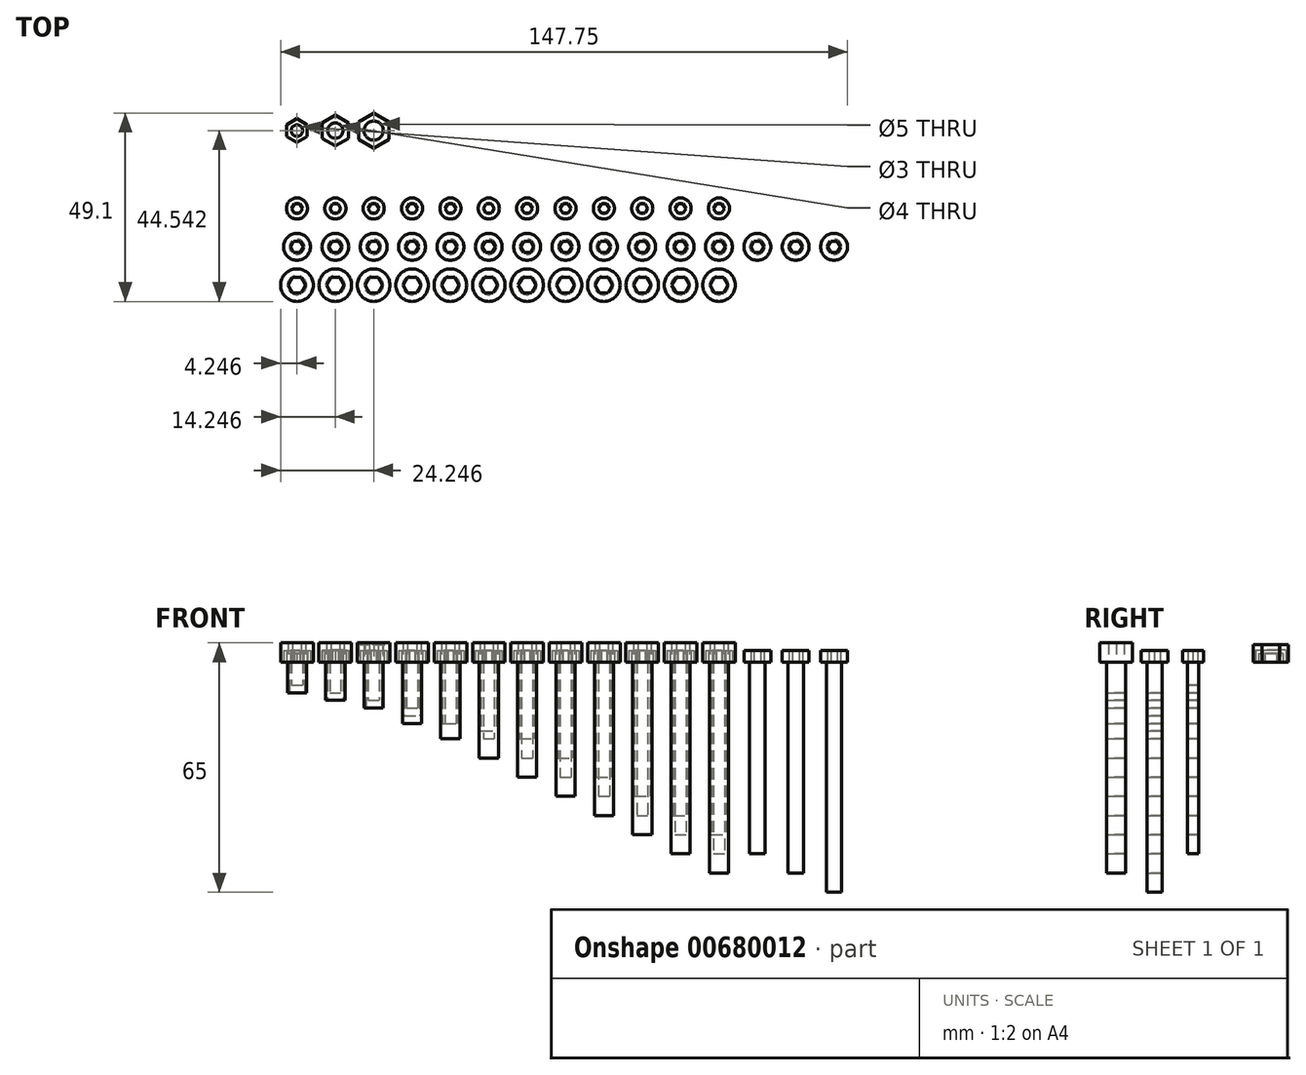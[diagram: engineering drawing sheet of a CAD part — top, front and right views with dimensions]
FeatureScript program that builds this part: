
annotation { "Feature Type Name" : "Feature", "Feature Type Description" : "" }
export const myFeature = defineFeature(function(context is Context, id is Id, definition is map)
    precondition{}
    {
        {
            var Q0;
            Q0=qCreatedBy(makeId("Top.planeOp"),FACE);
            var sketch = newSketch(context, id + "F0", { "sketchPlane" : qUnion([Q0])});
            skCircle(sketch, "E0", {"center": v(10, 10.3) * mm, "radius": 1.5 * mm});
            skLineSegment(sketch, "E1", {"start": v(0, 0) * mm, "end": v(0, 10) * mm, "construction": true});
            skLineSegment(sketch, "E2", {"start": v(0, 10) * mm, "end": v(10, 10.3) * mm, "construction": true});
            skLineSegment(sketch, "E3", {"start": v(10, 10.3) * mm, "end": v(20, 10.3) * mm, "construction": true});
            skLineSegment(sketch, "E4", {"start": v(20, 10.3) * mm, "end": v(30, 10.3) * mm, "construction": true});
            skLineSegment(sketch, "E5", {"start": v(30, 10.3) * mm, "end": v(40, 10.3) * mm, "construction": true});
            skCircle(sketch, "E6", {"center": v(20, 10.3) * mm, "radius": 2 * mm});
            skCircle(sketch, "E7", {"center": v(30, 10.3) * mm, "radius": 2.5 * mm});
            skCircle(sketch, "E8.cCircle", {"center": v(10, 10.3) * mm, "radius": 2.7 * mm, "construction": true});
            skLineSegment(sketch, "E8.0", {"start": v(12.7, 11.85) * mm, "end": v(12.7, 8.73) * mm});
            skLineSegment(sketch, "E8.1", {"start": v(12.7, 8.73) * mm, "end": v(10, 7.17) * mm});
            skLineSegment(sketch, "E8.2", {"start": v(10, 7.17) * mm, "end": v(7.3, 8.73) * mm});
            skLineSegment(sketch, "E8.3", {"start": v(7.3, 8.73) * mm, "end": v(7.3, 11.85) * mm});
            skLineSegment(sketch, "E8.4", {"start": v(7.3, 11.85) * mm, "end": v(10, 13.4) * mm});
            skLineSegment(sketch, "E8.5", {"start": v(10, 13.4) * mm, "end": v(12.7, 11.85) * mm});
            skPoint(sketch, "E8.0.midPoint", {"position": v(12.7, 10.3) * mm});
            skCircle(sketch, "E9.cCircle", {"center": v(20, 10.3) * mm, "radius": 3.45 * mm, "construction": true});
            skLineSegment(sketch, "E9.0", {"start": v(23.45, 12.28) * mm, "end": v(23.45, 8.3) * mm});
            skLineSegment(sketch, "E9.1", {"start": v(23.45, 8.3) * mm, "end": v(20, 6.3) * mm});
            skLineSegment(sketch, "E9.2", {"start": v(20, 6.3) * mm, "end": v(16.55, 8.3) * mm});
            skLineSegment(sketch, "E9.3", {"start": v(16.55, 8.3) * mm, "end": v(16.55, 12.28) * mm});
            skLineSegment(sketch, "E9.4", {"start": v(16.55, 12.28) * mm, "end": v(20, 14.28) * mm});
            skLineSegment(sketch, "E9.5", {"start": v(20, 14.28) * mm, "end": v(23.45, 12.28) * mm});
            skPoint(sketch, "E9.0.midPoint", {"position": v(23.45, 10.3) * mm});
            skCircle(sketch, "E10.cCircle", {"center": v(30, 10.3) * mm, "radius": 3.95 * mm, "construction": true});
            skLineSegment(sketch, "E10.0", {"start": v(33.95, 12.57) * mm, "end": v(33.95, 8.01) * mm});
            skLineSegment(sketch, "E10.1", {"start": v(33.95, 8.01) * mm, "end": v(30, 5.73) * mm});
            skLineSegment(sketch, "E10.2", {"start": v(30, 5.73) * mm, "end": v(26.05, 8.01) * mm});
            skLineSegment(sketch, "E10.3", {"start": v(26.05, 8.01) * mm, "end": v(26.05, 12.57) * mm});
            skLineSegment(sketch, "E10.4", {"start": v(26.05, 12.57) * mm, "end": v(30, 14.85) * mm});
            skLineSegment(sketch, "E10.5", {"start": v(30, 14.85) * mm, "end": v(33.95, 12.57) * mm});
            skPoint(sketch, "E10.0.midPoint", {"position": v(33.95, 10.3) * mm});
            skSolve(sketch);
        }
        {
            var Q0;
            Q0=makeQuery(id+"F0.imprint","IMPRINT",FACE,{"disambiguationData":[TD([[makeQuery(id+"F0.imprint","IMPRINT",EDGE,{"derivedFrom":sQuery(id+"F0.wireOp",EDGE,"E0")}),-1.0]])]});
            extrude(context, id + "F1", {"entities" : qUnion([Q0]), "depth" : 2.3 * mm});
        }
        {
            var Q0;
            Q0=makeQuery(id+"F0.imprint","IMPRINT",FACE,{"disambiguationData":[TD([[makeQuery(id+"F0.imprint","IMPRINT",EDGE,{"derivedFrom":sQuery(id+"F0.wireOp",EDGE,"E6")}),-1.0]])]});
            extrude(context, id + "F2", {"entities" : qUnion([Q0]), "depth" : 3.1 * mm});
        }
        {
            var Q0;
            Q0=makeQuery(id+"F0.imprint","IMPRINT",FACE,{"disambiguationData":[TD([[makeQuery(id+"F0.imprint","IMPRINT",EDGE,{"derivedFrom":sQuery(id+"F0.wireOp",EDGE,"E7")}),-1.0]])]});
            extrude(context, id + "F3", {"entities" : qUnion([Q0]), "depth" : 4.5 * mm});
        }
        {
            var Q0;
            Q0=qCreatedBy(makeId("Front.planeOp"),FACE);
            cPlane(context, id + "F4", {"entities" : qUnion([Q0]), "cplaneType" : CPlaneType.OFFSET, "offset" : 10 * mm, "width" : 150 * mm, "height" : 150 * mm});
        }
        {
            var Q0;
            Q0=qCreatedBy(id+"F4.planeOp",FACE);
            var sketch = newSketch(context, id + "F5", { "sketchPlane" : qUnion([Q0])});
            skLineSegment(sketch, "E11", {"start": v(10, 0) * mm, "end": v(0, 0) * mm, "construction": true});
            skLineSegment(sketch, "E12", {"start": v(10, 0) * mm, "end": v(20, 0) * mm, "construction": true});
            skLineSegment(sketch, "E13", {"start": v(0, 0) * mm, "end": v(0, 3) * mm, "construction": true});
            skLineSegment(sketch, "E14", {"start": v(0, 3) * mm, "end": v(153.62, 3) * mm, "construction": true});
            skLineSegment(sketch, "E15", {"start": v(10, 0) * mm, "end": v(10, 3) * mm});
            skLineSegment(sketch, "E16", {"start": v(10, 3) * mm, "end": v(12.75, 3) * mm});
            skLineSegment(sketch, "E17", {"start": v(12.75, 3) * mm, "end": v(12.75, 0) * mm});
            skLineSegment(sketch, "E18", {"start": v(12.75, 0) * mm, "end": v(11.45, 0) * mm});
            skLineSegment(sketch, "E19", {"start": v(11.45, 0) * mm, "end": v(11.45, -6) * mm});
            skLineSegment(sketch, "E20", {"start": v(11.45, -6) * mm, "end": v(10, -6) * mm});
            skLineSegment(sketch, "E21", {"start": v(10, -6) * mm, "end": v(10, 0) * mm});
            skLineSegment(sketch, "E22.1.0.0", {"start": v(22.75, 0) * mm, "end": v(21.45, 0) * mm});
            skLineSegment(sketch, "E22.1.0.1", {"start": v(20, 0) * mm, "end": v(20, 3) * mm});
            skLineSegment(sketch, "E22.1.0.2", {"start": v(20, 3) * mm, "end": v(22.75, 3) * mm});
            skLineSegment(sketch, "E22.1.0.3", {"start": v(22.75, 3) * mm, "end": v(22.75, 0) * mm});
            skLineSegment(sketch, "E22.1.0.4", {"start": v(20, 0) * mm, "end": v(30, 0) * mm, "construction": true});
            skLineSegment(sketch, "E22.2.0.0", {"start": v(32.75, 0) * mm, "end": v(31.45, 0) * mm});
            skLineSegment(sketch, "E22.2.0.1", {"start": v(30, 0) * mm, "end": v(30, 3) * mm});
            skLineSegment(sketch, "E22.2.0.2", {"start": v(30, 3) * mm, "end": v(32.75, 3) * mm});
            skLineSegment(sketch, "E22.2.0.3", {"start": v(32.75, 3) * mm, "end": v(32.75, 0) * mm});
            skLineSegment(sketch, "E22.2.0.4", {"start": v(30, 0) * mm, "end": v(40, 0) * mm, "construction": true});
            skLineSegment(sketch, "E22.3.0.0", {"start": v(42.75, 0) * mm, "end": v(41.45, 0) * mm});
            skLineSegment(sketch, "E22.3.0.1", {"start": v(40, 0) * mm, "end": v(40, 3) * mm});
            skLineSegment(sketch, "E22.3.0.2", {"start": v(40, 3) * mm, "end": v(42.75, 3) * mm});
            skLineSegment(sketch, "E22.3.0.3", {"start": v(42.75, 3) * mm, "end": v(42.75, 0) * mm});
            skLineSegment(sketch, "E22.3.0.4", {"start": v(40, 0) * mm, "end": v(50, 0) * mm, "construction": true});
            skLineSegment(sketch, "E22.4.0.0", {"start": v(52.75, 0) * mm, "end": v(51.45, 0) * mm});
            skLineSegment(sketch, "E22.4.0.1", {"start": v(50, 0) * mm, "end": v(50, 3) * mm});
            skLineSegment(sketch, "E22.4.0.2", {"start": v(50, 3) * mm, "end": v(52.75, 3) * mm});
            skLineSegment(sketch, "E22.4.0.3", {"start": v(52.75, 3) * mm, "end": v(52.75, 0) * mm});
            skLineSegment(sketch, "E22.4.0.4", {"start": v(50, 0) * mm, "end": v(60, 0) * mm, "construction": true});
            skLineSegment(sketch, "E22.5.0.0", {"start": v(62.75, 0) * mm, "end": v(61.45, 0) * mm});
            skLineSegment(sketch, "E22.5.0.1", {"start": v(60, 0) * mm, "end": v(60, 3) * mm});
            skLineSegment(sketch, "E22.5.0.2", {"start": v(60, 3) * mm, "end": v(62.75, 3) * mm});
            skLineSegment(sketch, "E22.5.0.3", {"start": v(62.75, 3) * mm, "end": v(62.75, 0) * mm});
            skLineSegment(sketch, "E22.5.0.4", {"start": v(60, 0) * mm, "end": v(70, 0) * mm, "construction": true});
            skLineSegment(sketch, "E22.6.0.0", {"start": v(72.75, 0) * mm, "end": v(71.45, 0) * mm});
            skLineSegment(sketch, "E22.6.0.1", {"start": v(70, 0) * mm, "end": v(70, 3) * mm});
            skLineSegment(sketch, "E22.6.0.2", {"start": v(70, 3) * mm, "end": v(72.75, 3) * mm});
            skLineSegment(sketch, "E22.6.0.3", {"start": v(72.75, 3) * mm, "end": v(72.75, 0) * mm});
            skLineSegment(sketch, "E22.6.0.4", {"start": v(70, 0) * mm, "end": v(80, 0) * mm, "construction": true});
            skLineSegment(sketch, "E22.7.0.0", {"start": v(82.75, 0) * mm, "end": v(81.45, 0) * mm});
            skLineSegment(sketch, "E22.7.0.1", {"start": v(80, 0) * mm, "end": v(80, 3) * mm});
            skLineSegment(sketch, "E22.7.0.2", {"start": v(80, 3) * mm, "end": v(82.75, 3) * mm});
            skLineSegment(sketch, "E22.7.0.3", {"start": v(82.75, 3) * mm, "end": v(82.75, 0) * mm});
            skLineSegment(sketch, "E22.7.0.4", {"start": v(80, 0) * mm, "end": v(90, 0) * mm, "construction": true});
            skLineSegment(sketch, "E22.8.0.0", {"start": v(92.75, 0) * mm, "end": v(91.45, 0) * mm});
            skLineSegment(sketch, "E22.8.0.1", {"start": v(90, 0) * mm, "end": v(90, 3) * mm});
            skLineSegment(sketch, "E22.8.0.2", {"start": v(90, 3) * mm, "end": v(92.75, 3) * mm});
            skLineSegment(sketch, "E22.8.0.3", {"start": v(92.75, 3) * mm, "end": v(92.75, 0) * mm});
            skLineSegment(sketch, "E22.8.0.4", {"start": v(90, 0) * mm, "end": v(100, 0) * mm, "construction": true});
            skLineSegment(sketch, "E22.9.0.0", {"start": v(102.75, 0) * mm, "end": v(101.45, 0) * mm});
            skLineSegment(sketch, "E22.9.0.1", {"start": v(100, 0) * mm, "end": v(100, 3) * mm});
            skLineSegment(sketch, "E22.9.0.2", {"start": v(100, 3) * mm, "end": v(102.75, 3) * mm});
            skLineSegment(sketch, "E22.9.0.3", {"start": v(102.75, 3) * mm, "end": v(102.75, 0) * mm});
            skLineSegment(sketch, "E22.9.0.4", {"start": v(100, 0) * mm, "end": v(110, 0) * mm, "construction": true});
            skLineSegment(sketch, "E22.direction1", {"start": v(11.45, 0) * mm, "end": v(21.45, 0) * mm, "construction": true});
            skLineSegment(sketch, "E23", {"start": v(21.45, 0) * mm, "end": v(21.45, -8) * mm});
            skLineSegment(sketch, "E24", {"start": v(21.45, -8) * mm, "end": v(20, -8) * mm});
            skLineSegment(sketch, "E25", {"start": v(20, -8) * mm, "end": v(20, 0) * mm});
            skLineSegment(sketch, "E26", {"start": v(30, 0) * mm, "end": v(30, -10) * mm});
            skLineSegment(sketch, "E27", {"start": v(30, -10) * mm, "end": v(31.45, -10) * mm});
            skLineSegment(sketch, "E28", {"start": v(31.45, -10) * mm, "end": v(31.45, 0) * mm});
            skLineSegment(sketch, "E29", {"start": v(40, 0) * mm, "end": v(40, -12) * mm});
            skLineSegment(sketch, "E30", {"start": v(40, -12) * mm, "end": v(41.45, -12) * mm});
            skLineSegment(sketch, "E31", {"start": v(41.45, -12) * mm, "end": v(41.45, 0) * mm});
            skLineSegment(sketch, "E32", {"start": v(50, 0) * mm, "end": v(50, -16) * mm});
            skLineSegment(sketch, "E33", {"start": v(50, -16) * mm, "end": v(51.45, -16) * mm});
            skLineSegment(sketch, "E34", {"start": v(51.45, -16) * mm, "end": v(51.45, 0) * mm});
            skLineSegment(sketch, "E35", {"start": v(60, 0) * mm, "end": v(60, -20) * mm});
            skLineSegment(sketch, "E36", {"start": v(60, -20) * mm, "end": v(61.45, -20) * mm});
            skLineSegment(sketch, "E37", {"start": v(61.45, -20) * mm, "end": v(61.45, 0) * mm});
            skLineSegment(sketch, "E38", {"start": v(70, 0) * mm, "end": v(70, -25) * mm});
            skLineSegment(sketch, "E39", {"start": v(70, -25) * mm, "end": v(71.45, -25) * mm});
            skLineSegment(sketch, "E40", {"start": v(71.45, -25) * mm, "end": v(71.45, 0) * mm});
            skLineSegment(sketch, "E41", {"start": v(80, 0) * mm, "end": v(80, -30) * mm});
            skLineSegment(sketch, "E42", {"start": v(80, -30) * mm, "end": v(81.45, -30) * mm});
            skLineSegment(sketch, "E43", {"start": v(81.45, -30) * mm, "end": v(81.45, 0) * mm});
            skLineSegment(sketch, "E44", {"start": v(90, 0) * mm, "end": v(90, -35) * mm});
            skLineSegment(sketch, "E45", {"start": v(90, -35) * mm, "end": v(91.45, -35) * mm});
            skLineSegment(sketch, "E46", {"start": v(91.45, -35) * mm, "end": v(91.45, 0) * mm});
            skLineSegment(sketch, "E47", {"start": v(100, 0) * mm, "end": v(100, -40) * mm});
            skLineSegment(sketch, "E48", {"start": v(100, -40) * mm, "end": v(101.45, -40) * mm});
            skLineSegment(sketch, "E49", {"start": v(101.45, -40) * mm, "end": v(101.45, 0) * mm});
            skLineSegment(sketch, "E50.0.10.0", {"start": v(112.75, 0) * mm, "end": v(111.45, 0) * mm});
            skLineSegment(sketch, "E50.3.10.0", {"start": v(110, 0) * mm, "end": v(110, 3) * mm});
            skLineSegment(sketch, "E50.6.10.0", {"start": v(110, 3) * mm, "end": v(112.75, 3) * mm});
            skLineSegment(sketch, "E50.9.10.0", {"start": v(112.75, 3) * mm, "end": v(112.75, 0) * mm});
            skLineSegment(sketch, "E50.12.10.0", {"start": v(110, 0) * mm, "end": v(120, 0) * mm, "construction": true});
            skLineSegment(sketch, "E50.0.11.0", {"start": v(122.75, 0) * mm, "end": v(121.45, 0) * mm});
            skLineSegment(sketch, "E50.3.11.0", {"start": v(120, 0) * mm, "end": v(120, 3) * mm});
            skLineSegment(sketch, "E50.6.11.0", {"start": v(120, 3) * mm, "end": v(122.75, 3) * mm});
            skLineSegment(sketch, "E50.9.11.0", {"start": v(122.75, 3) * mm, "end": v(122.75, 0) * mm});
            skLineSegment(sketch, "E50.12.11.0", {"start": v(120, 0) * mm, "end": v(130, 0) * mm, "construction": true});
            skLineSegment(sketch, "E51", {"start": v(110, 0) * mm, "end": v(110, -45) * mm});
            skLineSegment(sketch, "E52", {"start": v(110, -45) * mm, "end": v(111.45, -45) * mm});
            skLineSegment(sketch, "E53", {"start": v(111.45, -45) * mm, "end": v(111.45, 0) * mm});
            skLineSegment(sketch, "E54", {"start": v(120, 0) * mm, "end": v(120, -50) * mm});
            skLineSegment(sketch, "E55", {"start": v(120, -50) * mm, "end": v(121.45, -50) * mm});
            skLineSegment(sketch, "E56", {"start": v(121.45, -50) * mm, "end": v(121.45, 0) * mm});
            skSolve(sketch);
        }
        {
            var Q0;
            Q0=makeQuery(id+"F5.imprint","IMPRINT",FACE,{"disambiguationData":[TD([[makeQuery(id+"F5.imprint","IMPRINT",EDGE,{"derivedFrom":sQuery(id+"F5.wireOp",EDGE,"E15")}),-1.0]])]});
            var Q1;
            Q1=sQuery(id+"F5.wireOp",EDGE,"E15");
            revolve(context, id + "F6", {"entities" : qUnion([Q0]), "axis" : qUnion([Q1]), "revolveType" : RevolveType.FULL});
        }
        {
            var Q0;
            Q0=makeQuery(id+"F5.imprint","IMPRINT",FACE,{"disambiguationData":[TD([[makeQuery(id+"F5.imprint","IMPRINT",EDGE,{"derivedFrom":sQuery(id+"F5.wireOp",EDGE,"E22.1.0.0")}),-1.0]])]});
            var Q1;
            Q1=sQuery(id+"F5.wireOp",EDGE,"E22.1.0.1");
            revolve(context, id + "F7", {"entities" : qUnion([Q0]), "axis" : qUnion([Q1]), "revolveType" : RevolveType.FULL});
        }
        {
            var Q0;
            Q0=makeQuery(id+"F5.imprint","IMPRINT",FACE,{"disambiguationData":[TD([[makeQuery(id+"F5.imprint","IMPRINT",EDGE,{"derivedFrom":sQuery(id+"F5.wireOp",EDGE,"E22.2.0.0")}),-1.0]])]});
            var Q1;
            Q1=sQuery(id+"F5.wireOp",EDGE,"E22.2.0.1");
            revolve(context, id + "F8", {"entities" : qUnion([Q0]), "axis" : qUnion([Q1]), "revolveType" : RevolveType.FULL});
        }
        {
            var Q0;
            Q0=makeQuery(id+"F5.imprint","IMPRINT",FACE,{"disambiguationData":[TD([[makeQuery(id+"F5.imprint","IMPRINT",EDGE,{"derivedFrom":sQuery(id+"F5.wireOp",EDGE,"E22.3.0.0")}),-1.0]])]});
            var Q1;
            Q1=sQuery(id+"F5.wireOp",EDGE,"E22.3.0.1");
            revolve(context, id + "F9", {"entities" : qUnion([Q0]), "axis" : qUnion([Q1]), "revolveType" : RevolveType.FULL});
        }
        {
            var Q0;
            Q0=makeQuery(id+"F5.imprint","IMPRINT",FACE,{"disambiguationData":[TD([[makeQuery(id+"F5.imprint","IMPRINT",EDGE,{"derivedFrom":sQuery(id+"F5.wireOp",EDGE,"E22.4.0.0")}),-1.0]])]});
            var Q1;
            Q1=sQuery(id+"F5.wireOp",EDGE,"E22.4.0.1");
            revolve(context, id + "F10", {"entities" : qUnion([Q0]), "axis" : qUnion([Q1]), "revolveType" : RevolveType.FULL});
        }
        {
            var Q0;
            Q0=makeQuery(id+"F5.imprint","IMPRINT",FACE,{"disambiguationData":[TD([[makeQuery(id+"F5.imprint","IMPRINT",EDGE,{"derivedFrom":sQuery(id+"F5.wireOp",EDGE,"E22.5.0.0")}),-1.0]])]});
            var Q1;
            Q1=sQuery(id+"F5.wireOp",EDGE,"E22.5.0.1");
            revolve(context, id + "F11", {"entities" : qUnion([Q0]), "axis" : qUnion([Q1]), "revolveType" : RevolveType.FULL});
        }
        {
            var Q0;
            Q0=makeQuery(id+"F5.imprint","IMPRINT",FACE,{"disambiguationData":[TD([[makeQuery(id+"F5.imprint","IMPRINT",EDGE,{"derivedFrom":sQuery(id+"F5.wireOp",EDGE,"E22.6.0.0")}),-1.0]])]});
            var Q1;
            Q1=sQuery(id+"F5.wireOp",EDGE,"E22.6.0.1");
            revolve(context, id + "F12", {"entities" : qUnion([Q0]), "axis" : qUnion([Q1]), "revolveType" : RevolveType.FULL});
        }
        {
            var Q0;
            Q0=makeQuery(id+"F5.imprint","IMPRINT",FACE,{"disambiguationData":[TD([[makeQuery(id+"F5.imprint","IMPRINT",EDGE,{"derivedFrom":sQuery(id+"F5.wireOp",EDGE,"E22.7.0.0")}),-1.0]])]});
            var Q1;
            Q1=sQuery(id+"F5.wireOp",EDGE,"E22.7.0.1");
            revolve(context, id + "F13", {"entities" : qUnion([Q0]), "axis" : qUnion([Q1]), "revolveType" : RevolveType.FULL});
        }
        {
            var Q0;
            Q0=makeQuery(id+"F5.imprint","IMPRINT",FACE,{"disambiguationData":[TD([[makeQuery(id+"F5.imprint","IMPRINT",EDGE,{"derivedFrom":sQuery(id+"F5.wireOp",EDGE,"E22.8.0.0")}),-1.0]])]});
            var Q1;
            Q1=sQuery(id+"F5.wireOp",EDGE,"E22.8.0.1");
            revolve(context, id + "F14", {"entities" : qUnion([Q0]), "axis" : qUnion([Q1]), "revolveType" : RevolveType.FULL});
        }
        {
            var Q0;
            Q0=makeQuery(id+"F5.imprint","IMPRINT",FACE,{"disambiguationData":[TD([[makeQuery(id+"F5.imprint","IMPRINT",EDGE,{"derivedFrom":sQuery(id+"F5.wireOp",EDGE,"E22.9.0.0")}),-1.0]])]});
            var Q1;
            Q1=sQuery(id+"F5.wireOp",EDGE,"E22.9.0.1");
            revolve(context, id + "F15", {"entities" : qUnion([Q0]), "axis" : qUnion([Q1]), "revolveType" : RevolveType.FULL});
        }
        {
            var Q0;
            Q0=makeQuery(id+"F5.imprint","IMPRINT",FACE,{"disambiguationData":[TD([[makeQuery(id+"F5.imprint","IMPRINT",EDGE,{"derivedFrom":sQuery(id+"F5.wireOp",EDGE,"E50.0.10.0")}),-1.0]])]});
            var Q1;
            Q1=sQuery(id+"F5.wireOp",EDGE,"E50.3.10.0");
            revolve(context, id + "F16", {"entities" : qUnion([Q0]), "axis" : qUnion([Q1]), "revolveType" : RevolveType.FULL});
        }
        {
            var Q0;
            Q0=makeQuery(id+"F5.imprint","IMPRINT",FACE,{"disambiguationData":[TD([[makeQuery(id+"F5.imprint","IMPRINT",EDGE,{"derivedFrom":sQuery(id+"F5.wireOp",EDGE,"E50.0.11.0")}),-1.0]])]});
            var Q1;
            Q1=sQuery(id+"F5.wireOp",EDGE,"E50.3.11.0");
            revolve(context, id + "F17", {"entities" : qUnion([Q0]), "axis" : qUnion([Q1]), "revolveType" : RevolveType.FULL});
        }
        {
            var Q0;
            Q0=qCreatedBy(makeId("Front.planeOp"),FACE);
            cPlane(context, id + "F18", {"entities" : qUnion([Q0]), "cplaneType" : CPlaneType.OFFSET, "offset" : 20 * mm, "width" : 150 * mm, "height" : 150 * mm});
        }
        {
            var Q0;
            Q0=qCreatedBy(id+"F18.planeOp",FACE);
            var sketch = newSketch(context, id + "F19", { "sketchPlane" : qUnion([Q0])});
            skLineSegment(sketch, "E57", {"start": v(0, 0) * mm, "end": v(10, 0) * mm, "construction": true});
            skLineSegment(sketch, "E58", {"start": v(10, 0) * mm, "end": v(10, 3) * mm});
            skLineSegment(sketch, "E59", {"start": v(10, 3) * mm, "end": v(13.5, 3) * mm});
            skLineSegment(sketch, "E60", {"start": v(13.5, 3) * mm, "end": v(13.5, 0) * mm});
            skLineSegment(sketch, "E61", {"start": v(13.5, 0) * mm, "end": v(12, 0) * mm});
            skLineSegment(sketch, "E62.1.0.0", {"start": v(23.5, 0) * mm, "end": v(22, 0) * mm});
            skLineSegment(sketch, "E62.1.0.1", {"start": v(23.5, 3) * mm, "end": v(23.5, 0) * mm});
            skLineSegment(sketch, "E62.1.0.2", {"start": v(20, 0) * mm, "end": v(20, 3) * mm});
            skLineSegment(sketch, "E62.1.0.3", {"start": v(20, 3) * mm, "end": v(23.5, 3) * mm});
            skLineSegment(sketch, "E62.2.0.0", {"start": v(33.5, 0) * mm, "end": v(32, 0) * mm});
            skLineSegment(sketch, "E62.2.0.1", {"start": v(33.5, 3) * mm, "end": v(33.5, 0) * mm});
            skLineSegment(sketch, "E62.2.0.2", {"start": v(30, 0) * mm, "end": v(30, 3) * mm});
            skLineSegment(sketch, "E62.2.0.3", {"start": v(30, 3) * mm, "end": v(33.5, 3) * mm});
            skLineSegment(sketch, "E62.3.0.0", {"start": v(43.5, 0) * mm, "end": v(42, 0) * mm});
            skLineSegment(sketch, "E62.3.0.1", {"start": v(43.5, 3) * mm, "end": v(43.5, 0) * mm});
            skLineSegment(sketch, "E62.3.0.2", {"start": v(40, 0) * mm, "end": v(40, 3) * mm});
            skLineSegment(sketch, "E62.3.0.3", {"start": v(40, 3) * mm, "end": v(43.5, 3) * mm});
            skLineSegment(sketch, "E62.4.0.0", {"start": v(53.5, 0) * mm, "end": v(52, 0) * mm});
            skLineSegment(sketch, "E62.4.0.1", {"start": v(53.5, 3) * mm, "end": v(53.5, 0) * mm});
            skLineSegment(sketch, "E62.4.0.2", {"start": v(50, 0) * mm, "end": v(50, 3) * mm});
            skLineSegment(sketch, "E62.4.0.3", {"start": v(50, 3) * mm, "end": v(53.5, 3) * mm});
            skLineSegment(sketch, "E62.5.0.0", {"start": v(63.5, 0) * mm, "end": v(62, 0) * mm});
            skLineSegment(sketch, "E62.5.0.1", {"start": v(63.5, 3) * mm, "end": v(63.5, 0) * mm});
            skLineSegment(sketch, "E62.5.0.2", {"start": v(60, 0) * mm, "end": v(60, 3) * mm});
            skLineSegment(sketch, "E62.5.0.3", {"start": v(60, 3) * mm, "end": v(63.5, 3) * mm});
            skLineSegment(sketch, "E62.6.0.0", {"start": v(73.5, 0) * mm, "end": v(72, 0) * mm});
            skLineSegment(sketch, "E62.6.0.1", {"start": v(73.5, 3) * mm, "end": v(73.5, 0) * mm});
            skLineSegment(sketch, "E62.6.0.2", {"start": v(70, 0) * mm, "end": v(70, 3) * mm});
            skLineSegment(sketch, "E62.6.0.3", {"start": v(70, 3) * mm, "end": v(73.5, 3) * mm});
            skLineSegment(sketch, "E62.7.0.0", {"start": v(83.5, 0) * mm, "end": v(82, 0) * mm});
            skLineSegment(sketch, "E62.7.0.1", {"start": v(83.5, 3) * mm, "end": v(83.5, 0) * mm});
            skLineSegment(sketch, "E62.7.0.2", {"start": v(80, 0) * mm, "end": v(80, 3) * mm});
            skLineSegment(sketch, "E62.7.0.3", {"start": v(80, 3) * mm, "end": v(83.5, 3) * mm});
            skLineSegment(sketch, "E62.8.0.0", {"start": v(93.5, 0) * mm, "end": v(92, 0) * mm});
            skLineSegment(sketch, "E62.8.0.1", {"start": v(93.5, 3) * mm, "end": v(93.5, 0) * mm});
            skLineSegment(sketch, "E62.8.0.2", {"start": v(90, 0) * mm, "end": v(90, 3) * mm});
            skLineSegment(sketch, "E62.8.0.3", {"start": v(90, 3) * mm, "end": v(93.5, 3) * mm});
            skLineSegment(sketch, "E62.9.0.0", {"start": v(103.5, 0) * mm, "end": v(102, 0) * mm});
            skLineSegment(sketch, "E62.9.0.1", {"start": v(103.5, 3) * mm, "end": v(103.5, 0) * mm});
            skLineSegment(sketch, "E62.9.0.2", {"start": v(100, 0) * mm, "end": v(100, 3) * mm});
            skLineSegment(sketch, "E62.9.0.3", {"start": v(100, 3) * mm, "end": v(103.5, 3) * mm});
            skLineSegment(sketch, "E62.10.0.0", {"start": v(113.5, 0) * mm, "end": v(112, 0) * mm});
            skLineSegment(sketch, "E62.10.0.1", {"start": v(113.5, 3) * mm, "end": v(113.5, 0) * mm});
            skLineSegment(sketch, "E62.10.0.2", {"start": v(110, 0) * mm, "end": v(110, 3) * mm});
            skLineSegment(sketch, "E62.10.0.3", {"start": v(110, 3) * mm, "end": v(113.5, 3) * mm});
            skLineSegment(sketch, "E62.11.0.0", {"start": v(123.5, 0) * mm, "end": v(122, 0) * mm});
            skLineSegment(sketch, "E62.11.0.1", {"start": v(123.5, 3) * mm, "end": v(123.5, 0) * mm});
            skLineSegment(sketch, "E62.11.0.2", {"start": v(120, 0) * mm, "end": v(120, 3) * mm});
            skLineSegment(sketch, "E62.11.0.3", {"start": v(120, 3) * mm, "end": v(123.5, 3) * mm});
            skLineSegment(sketch, "E62.direction1", {"start": v(12, 0) * mm, "end": v(22, 0) * mm, "construction": true});
            skLineSegment(sketch, "E63", {"start": v(10, 0) * mm, "end": v(10, -8) * mm});
            skLineSegment(sketch, "E64", {"start": v(10, -8) * mm, "end": v(12, -8) * mm});
            skLineSegment(sketch, "E65", {"start": v(12, -8) * mm, "end": v(12, 0) * mm});
            skLineSegment(sketch, "E66", {"start": v(20, 0) * mm, "end": v(20, -10) * mm});
            skLineSegment(sketch, "E67", {"start": v(20, -10) * mm, "end": v(22, -10) * mm});
            skLineSegment(sketch, "E68", {"start": v(22, -10) * mm, "end": v(22, 0) * mm});
            skLineSegment(sketch, "E69", {"start": v(30, 0) * mm, "end": v(30, -12) * mm});
            skLineSegment(sketch, "E70", {"start": v(30, -12) * mm, "end": v(32, -12) * mm});
            skLineSegment(sketch, "E71", {"start": v(32, -12) * mm, "end": v(32, 0) * mm});
            skLineSegment(sketch, "E72", {"start": v(40, 0) * mm, "end": v(40, -14) * mm});
            skLineSegment(sketch, "E73", {"start": v(40, -14) * mm, "end": v(42, -14) * mm});
            skLineSegment(sketch, "E74", {"start": v(42, -14) * mm, "end": v(42, 0) * mm});
            skLineSegment(sketch, "E75", {"start": v(50, 0) * mm, "end": v(50, -16) * mm});
            skLineSegment(sketch, "E76", {"start": v(50, -16) * mm, "end": v(52, -16) * mm});
            skLineSegment(sketch, "E77", {"start": v(52, -16) * mm, "end": v(52, 0) * mm});
            skLineSegment(sketch, "E78", {"start": v(60, 0) * mm, "end": v(60, -18) * mm});
            skLineSegment(sketch, "E79", {"start": v(60, -18) * mm, "end": v(62, -18) * mm});
            skLineSegment(sketch, "E80", {"start": v(62, -18) * mm, "end": v(62, 0) * mm});
            skLineSegment(sketch, "E81", {"start": v(70, 0) * mm, "end": v(70, -20) * mm});
            skLineSegment(sketch, "E82", {"start": v(70, -20) * mm, "end": v(72, -20) * mm});
            skLineSegment(sketch, "E83", {"start": v(72, -20) * mm, "end": v(72, 0) * mm});
            skLineSegment(sketch, "E84", {"start": v(80, 0) * mm, "end": v(80, -25) * mm});
            skLineSegment(sketch, "E85", {"start": v(80, -25) * mm, "end": v(82, -25) * mm});
            skLineSegment(sketch, "E86", {"start": v(82, -25) * mm, "end": v(82, 0) * mm});
            skLineSegment(sketch, "E87", {"start": v(90, 0) * mm, "end": v(90, -30) * mm});
            skLineSegment(sketch, "E88", {"start": v(90, -30) * mm, "end": v(92, -30) * mm});
            skLineSegment(sketch, "E89", {"start": v(92, -30) * mm, "end": v(92, 0) * mm});
            skLineSegment(sketch, "E90", {"start": v(100, 0) * mm, "end": v(100, -35) * mm});
            skLineSegment(sketch, "E91", {"start": v(100, -35) * mm, "end": v(102, -35) * mm});
            skLineSegment(sketch, "E92", {"start": v(102, -35) * mm, "end": v(102, 0) * mm});
            skLineSegment(sketch, "E93", {"start": v(110, 0) * mm, "end": v(110, -40) * mm});
            skLineSegment(sketch, "E94", {"start": v(110, -40) * mm, "end": v(112, -40) * mm});
            skLineSegment(sketch, "E95", {"start": v(112, -40) * mm, "end": v(112, 0) * mm});
            skLineSegment(sketch, "E96", {"start": v(120, 0) * mm, "end": v(120, -45) * mm});
            skLineSegment(sketch, "E97", {"start": v(120, -45) * mm, "end": v(122, -45) * mm});
            skLineSegment(sketch, "E98", {"start": v(122, -45) * mm, "end": v(122, 0) * mm});
            skLineSegment(sketch, "E99.0.12.0", {"start": v(133.5, 0) * mm, "end": v(132, 0) * mm});
            skLineSegment(sketch, "E99.3.12.0", {"start": v(133.5, 3) * mm, "end": v(133.5, 0) * mm});
            skLineSegment(sketch, "E99.6.12.0", {"start": v(130, 0) * mm, "end": v(130, 3) * mm});
            skLineSegment(sketch, "E99.9.12.0", {"start": v(130, 3) * mm, "end": v(133.5, 3) * mm});
            skLineSegment(sketch, "E100", {"start": v(130, 0) * mm, "end": v(130, -50) * mm});
            skLineSegment(sketch, "E101", {"start": v(130, -50) * mm, "end": v(132, -50) * mm});
            skLineSegment(sketch, "E102", {"start": v(132, -50) * mm, "end": v(132, 0) * mm});
            skLineSegment(sketch, "E103.0.13.0", {"start": v(143.5, 0) * mm, "end": v(142, 0) * mm});
            skLineSegment(sketch, "E103.3.13.0", {"start": v(143.5, 3) * mm, "end": v(143.5, 0) * mm});
            skLineSegment(sketch, "E103.6.13.0", {"start": v(140, 0) * mm, "end": v(140, 3) * mm});
            skLineSegment(sketch, "E103.9.13.0", {"start": v(140, 3) * mm, "end": v(143.5, 3) * mm});
            skLineSegment(sketch, "E103.0.14.0", {"start": v(153.5, 0) * mm, "end": v(152, 0) * mm});
            skLineSegment(sketch, "E103.3.14.0", {"start": v(153.5, 3) * mm, "end": v(153.5, 0) * mm});
            skLineSegment(sketch, "E103.6.14.0", {"start": v(150, 0) * mm, "end": v(150, 3) * mm});
            skLineSegment(sketch, "E103.9.14.0", {"start": v(150, 3) * mm, "end": v(153.5, 3) * mm});
            skLineSegment(sketch, "E104", {"start": v(140, 0) * mm, "end": v(140, -55) * mm});
            skLineSegment(sketch, "E105", {"start": v(140, -55) * mm, "end": v(142, -55) * mm});
            skLineSegment(sketch, "E106", {"start": v(142, -55) * mm, "end": v(142, 0) * mm});
            skLineSegment(sketch, "E107", {"start": v(150, 0) * mm, "end": v(150, -60) * mm});
            skLineSegment(sketch, "E108", {"start": v(150, -60) * mm, "end": v(152, -60) * mm});
            skLineSegment(sketch, "E109", {"start": v(152, -60) * mm, "end": v(152, 0) * mm});
            skSolve(sketch);
        }
        {
            var Q0;
            Q0=makeQuery(id+"F19.imprint","IMPRINT",FACE,{"disambiguationData":[TD([[makeQuery(id+"F19.imprint","IMPRINT",EDGE,{"derivedFrom":sQuery(id+"F19.wireOp",EDGE,"E58")}),-1.0]])]});
            var Q1;
            Q1=sQuery(id+"F19.wireOp",EDGE,"E58");
            revolve(context, id + "F20", {"entities" : qUnion([Q0]), "axis" : qUnion([Q1]), "revolveType" : RevolveType.FULL});
        }
        {
            var Q0;
            Q0=makeQuery(id+"F19.imprint","IMPRINT",FACE,{"disambiguationData":[TD([[makeQuery(id+"F19.imprint","IMPRINT",EDGE,{"derivedFrom":sQuery(id+"F19.wireOp",EDGE,"E62.1.0.0")}),-1.0]])]});
            var Q1;
            Q1=sQuery(id+"F19.wireOp",EDGE,"E62.1.0.2");
            revolve(context, id + "F21", {"entities" : qUnion([Q0]), "axis" : qUnion([Q1]), "revolveType" : RevolveType.FULL});
        }
        {
            var Q0;
            Q0=makeQuery(id+"F19.imprint","IMPRINT",FACE,{"disambiguationData":[TD([[makeQuery(id+"F19.imprint","IMPRINT",EDGE,{"derivedFrom":sQuery(id+"F19.wireOp",EDGE,"E62.2.0.0")}),-1.0]])]});
            var Q1;
            Q1=sQuery(id+"F19.wireOp",EDGE,"E62.2.0.2");
            revolve(context, id + "F22", {"entities" : qUnion([Q0]), "axis" : qUnion([Q1]), "revolveType" : RevolveType.FULL});
        }
        {
            var Q0;
            Q0=makeQuery(id+"F19.imprint","IMPRINT",FACE,{"disambiguationData":[TD([[makeQuery(id+"F19.imprint","IMPRINT",EDGE,{"derivedFrom":sQuery(id+"F19.wireOp",EDGE,"E62.3.0.0")}),-1.0]])]});
            var Q1;
            Q1=sQuery(id+"F19.wireOp",EDGE,"E62.3.0.2");
            revolve(context, id + "F23", {"entities" : qUnion([Q0]), "axis" : qUnion([Q1]), "revolveType" : RevolveType.FULL});
        }
        {
            var Q0;
            Q0=makeQuery(id+"F19.imprint","IMPRINT",FACE,{"disambiguationData":[TD([[makeQuery(id+"F19.imprint","IMPRINT",EDGE,{"derivedFrom":sQuery(id+"F19.wireOp",EDGE,"E62.4.0.0")}),-1.0]])]});
            var Q1;
            Q1=sQuery(id+"F19.wireOp",EDGE,"E62.4.0.2");
            revolve(context, id + "F24", {"entities" : qUnion([Q0]), "axis" : qUnion([Q1]), "revolveType" : RevolveType.FULL});
        }
        {
            var Q0;
            Q0=makeQuery(id+"F19.imprint","IMPRINT",FACE,{"disambiguationData":[TD([[makeQuery(id+"F19.imprint","IMPRINT",EDGE,{"derivedFrom":sQuery(id+"F19.wireOp",EDGE,"E62.5.0.0")}),-1.0]])]});
            var Q1;
            Q1=sQuery(id+"F19.wireOp",EDGE,"E62.5.0.2");
            revolve(context, id + "F25", {"entities" : qUnion([Q0]), "axis" : qUnion([Q1]), "revolveType" : RevolveType.FULL});
        }
        {
            var Q0;
            Q0=makeQuery(id+"F19.imprint","IMPRINT",FACE,{"disambiguationData":[TD([[makeQuery(id+"F19.imprint","IMPRINT",EDGE,{"derivedFrom":sQuery(id+"F19.wireOp",EDGE,"E62.6.0.0")}),-1.0]])]});
            var Q1;
            Q1=sQuery(id+"F19.wireOp",EDGE,"E62.6.0.2");
            revolve(context, id + "F26", {"entities" : qUnion([Q0]), "axis" : qUnion([Q1]), "revolveType" : RevolveType.FULL});
        }
        {
            var Q0;
            Q0=makeQuery(id+"F19.imprint","IMPRINT",FACE,{"disambiguationData":[TD([[makeQuery(id+"F19.imprint","IMPRINT",EDGE,{"derivedFrom":sQuery(id+"F19.wireOp",EDGE,"E62.7.0.0")}),-1.0]])]});
            var Q1;
            Q1=sQuery(id+"F19.wireOp",EDGE,"E62.7.0.2");
            revolve(context, id + "F27", {"entities" : qUnion([Q0]), "axis" : qUnion([Q1]), "revolveType" : RevolveType.FULL});
        }
        {
            var Q0;
            Q0=makeQuery(id+"F19.imprint","IMPRINT",FACE,{"disambiguationData":[TD([[makeQuery(id+"F19.imprint","IMPRINT",EDGE,{"derivedFrom":sQuery(id+"F19.wireOp",EDGE,"E62.8.0.0")}),-1.0]])]});
            var Q1;
            Q1=sQuery(id+"F19.wireOp",EDGE,"E62.8.0.2");
            revolve(context, id + "F28", {"entities" : qUnion([Q0]), "axis" : qUnion([Q1]), "revolveType" : RevolveType.FULL});
        }
        {
            var Q0;
            Q0=makeQuery(id+"F19.imprint","IMPRINT",FACE,{"disambiguationData":[TD([[makeQuery(id+"F19.imprint","IMPRINT",EDGE,{"derivedFrom":sQuery(id+"F19.wireOp",EDGE,"E62.9.0.0")}),-1.0]])]});
            var Q1;
            Q1=sQuery(id+"F19.wireOp",EDGE,"E62.9.0.2");
            revolve(context, id + "F29", {"entities" : qUnion([Q0]), "axis" : qUnion([Q1]), "revolveType" : RevolveType.FULL});
        }
        {
            var Q0;
            Q0=makeQuery(id+"F19.imprint","IMPRINT",FACE,{"disambiguationData":[TD([[makeQuery(id+"F19.imprint","IMPRINT",EDGE,{"derivedFrom":sQuery(id+"F19.wireOp",EDGE,"E62.10.0.0")}),-1.0]])]});
            var Q1;
            Q1=sQuery(id+"F19.wireOp",EDGE,"E62.10.0.2");
            revolve(context, id + "F30", {"entities" : qUnion([Q0]), "axis" : qUnion([Q1]), "revolveType" : RevolveType.FULL});
        }
        {
            var Q0;
            Q0=makeQuery(id+"F19.imprint","IMPRINT",FACE,{"disambiguationData":[TD([[makeQuery(id+"F19.imprint","IMPRINT",EDGE,{"derivedFrom":sQuery(id+"F19.wireOp",EDGE,"E62.11.0.0")}),-1.0]])]});
            var Q1;
            Q1=sQuery(id+"F19.wireOp",EDGE,"E62.11.0.2");
            revolve(context, id + "F31", {"entities" : qUnion([Q0]), "axis" : qUnion([Q1]), "revolveType" : RevolveType.FULL});
        }
        {
            var Q0;
            Q0=makeQuery(id+"F19.imprint","IMPRINT",FACE,{"disambiguationData":[TD([[makeQuery(id+"F19.imprint","IMPRINT",EDGE,{"derivedFrom":sQuery(id+"F19.wireOp",EDGE,"E99.0.12.0")}),-1.0]])]});
            var Q1;
            Q1=sQuery(id+"F19.wireOp",EDGE,"E99.6.12.0");
            revolve(context, id + "F32", {"entities" : qUnion([Q0]), "axis" : qUnion([Q1]), "revolveType" : RevolveType.FULL});
        }
        {
            var Q0;
            Q0=makeQuery(id+"F19.imprint","IMPRINT",FACE,{"disambiguationData":[TD([[makeQuery(id+"F19.imprint","IMPRINT",EDGE,{"derivedFrom":sQuery(id+"F19.wireOp",EDGE,"E103.0.13.0")}),-1.0]])]});
            var Q1;
            Q1=sQuery(id+"F19.wireOp",EDGE,"E103.6.13.0");
            revolve(context, id + "F33", {"entities" : qUnion([Q0]), "axis" : qUnion([Q1]), "revolveType" : RevolveType.FULL});
        }
        {
            var Q0;
            Q0=makeQuery(id+"F19.imprint","IMPRINT",FACE,{"disambiguationData":[TD([[makeQuery(id+"F19.imprint","IMPRINT",EDGE,{"derivedFrom":sQuery(id+"F19.wireOp",EDGE,"E103.0.14.0")}),-1.0]])]});
            var Q1;
            Q1=sQuery(id+"F19.wireOp",EDGE,"E103.6.14.0");
            revolve(context, id + "F34", {"entities" : qUnion([Q0]), "axis" : qUnion([Q1]), "revolveType" : RevolveType.FULL});
        }
        {
            var Q0;
            Q0=qCreatedBy(makeId("Front.planeOp"),FACE);
            cPlane(context, id + "F35", {"entities" : qUnion([Q0]), "cplaneType" : CPlaneType.OFFSET, "offset" : 30 * mm, "width" : 150 * mm, "height" : 150 * mm});
        }
        {
            var Q0;
            Q0=qCreatedBy(id+"F35.planeOp",FACE);
            var sketch = newSketch(context, id + "F36", { "sketchPlane" : qUnion([Q0])});
            skLineSegment(sketch, "E110", {"start": v(0, 0) * mm, "end": v(10, 0) * mm, "construction": true});
            skLineSegment(sketch, "E111", {"start": v(10, 0) * mm, "end": v(10, 5) * mm});
            skLineSegment(sketch, "E112", {"start": v(10, 5) * mm, "end": v(14.25, 5) * mm});
            skLineSegment(sketch, "E113", {"start": v(14.25, 5) * mm, "end": v(14.25, 0) * mm});
            skLineSegment(sketch, "E114", {"start": v(14.25, 0) * mm, "end": v(12.5, 0) * mm});
            skLineSegment(sketch, "E115", {"start": v(12.5, 0) * mm, "end": v(12.5, -8) * mm});
            skLineSegment(sketch, "E116", {"start": v(12.5, -8) * mm, "end": v(10, -8) * mm});
            skLineSegment(sketch, "E117", {"start": v(10, -8) * mm, "end": v(10, 0) * mm});
            skLineSegment(sketch, "E118", {"start": v(10, 0) * mm, "end": v(12.5, 0) * mm, "construction": true});
            skLineSegment(sketch, "E119.1.0.0", {"start": v(20, 0) * mm, "end": v(20, 5) * mm});
            skLineSegment(sketch, "E119.1.0.1", {"start": v(24.25, 5) * mm, "end": v(24.25, 0) * mm});
            skLineSegment(sketch, "E119.1.0.2", {"start": v(20, 5) * mm, "end": v(24.25, 5) * mm});
            skLineSegment(sketch, "E119.1.0.3", {"start": v(24.25, 0) * mm, "end": v(22.5, 0) * mm});
            skLineSegment(sketch, "E119.1.0.4", {"start": v(20, 0) * mm, "end": v(22.5, 0) * mm, "construction": true});
            skLineSegment(sketch, "E119.2.0.0", {"start": v(30, 0) * mm, "end": v(30, 5) * mm});
            skLineSegment(sketch, "E119.2.0.1", {"start": v(34.25, 5) * mm, "end": v(34.25, 0) * mm});
            skLineSegment(sketch, "E119.2.0.2", {"start": v(30, 5) * mm, "end": v(34.25, 5) * mm});
            skLineSegment(sketch, "E119.2.0.3", {"start": v(34.25, 0) * mm, "end": v(32.5, 0) * mm});
            skLineSegment(sketch, "E119.2.0.4", {"start": v(30, 0) * mm, "end": v(32.5, 0) * mm, "construction": true});
            skLineSegment(sketch, "E119.3.0.0", {"start": v(40, 0) * mm, "end": v(40, 5) * mm});
            skLineSegment(sketch, "E119.3.0.1", {"start": v(44.25, 5) * mm, "end": v(44.25, 0) * mm});
            skLineSegment(sketch, "E119.3.0.2", {"start": v(40, 5) * mm, "end": v(44.25, 5) * mm});
            skLineSegment(sketch, "E119.3.0.3", {"start": v(44.25, 0) * mm, "end": v(42.5, 0) * mm});
            skLineSegment(sketch, "E119.3.0.4", {"start": v(40, 0) * mm, "end": v(42.5, 0) * mm, "construction": true});
            skLineSegment(sketch, "E119.4.0.0", {"start": v(50, 0) * mm, "end": v(50, 5) * mm});
            skLineSegment(sketch, "E119.4.0.1", {"start": v(54.25, 5) * mm, "end": v(54.25, 0) * mm});
            skLineSegment(sketch, "E119.4.0.2", {"start": v(50, 5) * mm, "end": v(54.25, 5) * mm});
            skLineSegment(sketch, "E119.4.0.3", {"start": v(54.25, 0) * mm, "end": v(52.5, 0) * mm});
            skLineSegment(sketch, "E119.4.0.4", {"start": v(50, 0) * mm, "end": v(52.5, 0) * mm, "construction": true});
            skLineSegment(sketch, "E119.5.0.0", {"start": v(60, 0) * mm, "end": v(60, 5) * mm});
            skLineSegment(sketch, "E119.5.0.1", {"start": v(64.25, 5) * mm, "end": v(64.25, 0) * mm});
            skLineSegment(sketch, "E119.5.0.2", {"start": v(60, 5) * mm, "end": v(64.25, 5) * mm});
            skLineSegment(sketch, "E119.5.0.3", {"start": v(64.25, 0) * mm, "end": v(62.5, 0) * mm});
            skLineSegment(sketch, "E119.5.0.4", {"start": v(60, 0) * mm, "end": v(62.5, 0) * mm, "construction": true});
            skLineSegment(sketch, "E119.6.0.0", {"start": v(70, 0) * mm, "end": v(70, 5) * mm});
            skLineSegment(sketch, "E119.6.0.1", {"start": v(74.25, 5) * mm, "end": v(74.25, 0) * mm});
            skLineSegment(sketch, "E119.6.0.2", {"start": v(70, 5) * mm, "end": v(74.25, 5) * mm});
            skLineSegment(sketch, "E119.6.0.3", {"start": v(74.25, 0) * mm, "end": v(72.5, 0) * mm});
            skLineSegment(sketch, "E119.6.0.4", {"start": v(70, 0) * mm, "end": v(72.5, 0) * mm, "construction": true});
            skLineSegment(sketch, "E119.7.0.0", {"start": v(80, 0) * mm, "end": v(80, 5) * mm});
            skLineSegment(sketch, "E119.7.0.1", {"start": v(84.25, 5) * mm, "end": v(84.25, 0) * mm});
            skLineSegment(sketch, "E119.7.0.2", {"start": v(80, 5) * mm, "end": v(84.25, 5) * mm});
            skLineSegment(sketch, "E119.7.0.3", {"start": v(84.25, 0) * mm, "end": v(82.5, 0) * mm});
            skLineSegment(sketch, "E119.7.0.4", {"start": v(80, 0) * mm, "end": v(82.5, 0) * mm, "construction": true});
            skLineSegment(sketch, "E119.8.0.0", {"start": v(90, 0) * mm, "end": v(90, 5) * mm});
            skLineSegment(sketch, "E119.8.0.1", {"start": v(94.25, 5) * mm, "end": v(94.25, 0) * mm});
            skLineSegment(sketch, "E119.8.0.2", {"start": v(90, 5) * mm, "end": v(94.25, 5) * mm});
            skLineSegment(sketch, "E119.8.0.3", {"start": v(94.25, 0) * mm, "end": v(92.5, 0) * mm});
            skLineSegment(sketch, "E119.8.0.4", {"start": v(90, 0) * mm, "end": v(92.5, 0) * mm, "construction": true});
            skLineSegment(sketch, "E119.9.0.0", {"start": v(100, 0) * mm, "end": v(100, 5) * mm});
            skLineSegment(sketch, "E119.9.0.1", {"start": v(104.25, 5) * mm, "end": v(104.25, 0) * mm});
            skLineSegment(sketch, "E119.9.0.2", {"start": v(100, 5) * mm, "end": v(104.25, 5) * mm});
            skLineSegment(sketch, "E119.9.0.3", {"start": v(104.25, 0) * mm, "end": v(102.5, 0) * mm});
            skLineSegment(sketch, "E119.9.0.4", {"start": v(100, 0) * mm, "end": v(102.5, 0) * mm, "construction": true});
            skLineSegment(sketch, "E119.10.0.0", {"start": v(110, 0) * mm, "end": v(110, 5) * mm});
            skLineSegment(sketch, "E119.10.0.1", {"start": v(114.25, 5) * mm, "end": v(114.25, 0) * mm});
            skLineSegment(sketch, "E119.10.0.2", {"start": v(110, 5) * mm, "end": v(114.25, 5) * mm});
            skLineSegment(sketch, "E119.10.0.3", {"start": v(114.25, 0) * mm, "end": v(112.5, 0) * mm});
            skLineSegment(sketch, "E119.10.0.4", {"start": v(110, 0) * mm, "end": v(112.5, 0) * mm, "construction": true});
            skLineSegment(sketch, "E119.11.0.0", {"start": v(120, 0) * mm, "end": v(120, 5) * mm});
            skLineSegment(sketch, "E119.11.0.1", {"start": v(124.25, 5) * mm, "end": v(124.25, 0) * mm});
            skLineSegment(sketch, "E119.11.0.2", {"start": v(120, 5) * mm, "end": v(124.25, 5) * mm});
            skLineSegment(sketch, "E119.11.0.3", {"start": v(124.25, 0) * mm, "end": v(122.5, 0) * mm});
            skLineSegment(sketch, "E119.11.0.4", {"start": v(120, 0) * mm, "end": v(122.5, 0) * mm, "construction": true});
            skLineSegment(sketch, "E119.direction1", {"start": v(10, 0) * mm, "end": v(20, 0) * mm, "construction": true});
            skLineSegment(sketch, "E120", {"start": v(20, 0) * mm, "end": v(20, -10) * mm});
            skLineSegment(sketch, "E121", {"start": v(20, -10) * mm, "end": v(22.5, -10) * mm});
            skLineSegment(sketch, "E122", {"start": v(22.5, -10) * mm, "end": v(22.5, 0) * mm});
            skLineSegment(sketch, "E123", {"start": v(30, 0) * mm, "end": v(30, -12) * mm});
            skLineSegment(sketch, "E124", {"start": v(30, -12) * mm, "end": v(32.5, -12) * mm});
            skLineSegment(sketch, "E125", {"start": v(32.5, -12) * mm, "end": v(32.5, 0) * mm});
            skLineSegment(sketch, "E126", {"start": v(40, 0) * mm, "end": v(40, -16) * mm});
            skLineSegment(sketch, "E127", {"start": v(40, -16) * mm, "end": v(42.5, -16) * mm});
            skLineSegment(sketch, "E128", {"start": v(42.5, -16) * mm, "end": v(42.5, 0) * mm});
            skLineSegment(sketch, "E129", {"start": v(50, 0) * mm, "end": v(50, -20) * mm});
            skLineSegment(sketch, "E130", {"start": v(50, -20) * mm, "end": v(52.5, -20) * mm});
            skLineSegment(sketch, "E131", {"start": v(52.5, -20) * mm, "end": v(52.5, 0) * mm});
            skLineSegment(sketch, "E132", {"start": v(60, 0) * mm, "end": v(60, -25) * mm});
            skLineSegment(sketch, "E133", {"start": v(60, -25) * mm, "end": v(62.5, -25) * mm});
            skLineSegment(sketch, "E134", {"start": v(62.5, -25) * mm, "end": v(62.5, 0) * mm});
            skLineSegment(sketch, "E135", {"start": v(70, 0) * mm, "end": v(70, -30) * mm});
            skLineSegment(sketch, "E136", {"start": v(70, -30) * mm, "end": v(72.5, -30) * mm});
            skLineSegment(sketch, "E137", {"start": v(72.5, -30) * mm, "end": v(72.5, 0) * mm});
            skLineSegment(sketch, "E138", {"start": v(80, 0) * mm, "end": v(80, -35) * mm});
            skLineSegment(sketch, "E139", {"start": v(80, -35) * mm, "end": v(82.5, -35) * mm});
            skLineSegment(sketch, "E140", {"start": v(82.5, -35) * mm, "end": v(82.5, 0) * mm});
            skLineSegment(sketch, "E141", {"start": v(90, 0) * mm, "end": v(90, -40) * mm});
            skLineSegment(sketch, "E142", {"start": v(90, -40) * mm, "end": v(92.5, -40) * mm});
            skLineSegment(sketch, "E143", {"start": v(92.5, -40) * mm, "end": v(92.5, 0) * mm});
            skLineSegment(sketch, "E144", {"start": v(100, 0) * mm, "end": v(100, -45) * mm});
            skLineSegment(sketch, "E145", {"start": v(100, -45) * mm, "end": v(102.5, -45) * mm});
            skLineSegment(sketch, "E146", {"start": v(102.5, -45) * mm, "end": v(102.5, 0) * mm});
            skLineSegment(sketch, "E147", {"start": v(110, 0) * mm, "end": v(110, -50) * mm});
            skLineSegment(sketch, "E148", {"start": v(110, -50) * mm, "end": v(112.5, -50) * mm});
            skLineSegment(sketch, "E149", {"start": v(112.5, -50) * mm, "end": v(112.5, 0) * mm});
            skLineSegment(sketch, "E150", {"start": v(120, 0) * mm, "end": v(120, -55) * mm});
            skLineSegment(sketch, "E151", {"start": v(120, -55) * mm, "end": v(122.5, -55) * mm});
            skLineSegment(sketch, "E152", {"start": v(122.5, -55) * mm, "end": v(122.5, 0) * mm});
            skSolve(sketch);
        }
        {
            var Q0;
            Q0=makeQuery(id+"F36.imprint","IMPRINT",FACE,{"disambiguationData":[TD([[makeQuery(id+"F36.imprint","IMPRINT",EDGE,{"derivedFrom":sQuery(id+"F36.wireOp",EDGE,"E111")}),-1.0]])]});
            var Q1;
            Q1=sQuery(id+"F36.wireOp",EDGE,"E111");
            revolve(context, id + "F37", {"entities" : qUnion([Q0]), "axis" : qUnion([Q1]), "revolveType" : RevolveType.FULL});
        }
        {
            var Q0;
            Q0=makeQuery(id+"F36.imprint","IMPRINT",FACE,{"disambiguationData":[TD([[makeQuery(id+"F36.imprint","IMPRINT",EDGE,{"derivedFrom":sQuery(id+"F36.wireOp",EDGE,"E119.1.0.0")}),-1.0]])]});
            var Q1;
            Q1=sQuery(id+"F36.wireOp",EDGE,"E119.1.0.0");
            revolve(context, id + "F38", {"entities" : qUnion([Q0]), "axis" : qUnion([Q1]), "revolveType" : RevolveType.FULL});
        }
        {
            var Q0;
            Q0=makeQuery(id+"F36.imprint","IMPRINT",FACE,{"disambiguationData":[TD([[makeQuery(id+"F36.imprint","IMPRINT",EDGE,{"derivedFrom":sQuery(id+"F36.wireOp",EDGE,"E119.2.0.0")}),-1.0]])]});
            var Q1;
            Q1=sQuery(id+"F36.wireOp",EDGE,"E119.2.0.0");
            revolve(context, id + "F39", {"entities" : qUnion([Q0]), "axis" : qUnion([Q1]), "revolveType" : RevolveType.FULL});
        }
        {
            var Q0;
            Q0=makeQuery(id+"F36.imprint","IMPRINT",FACE,{"disambiguationData":[TD([[makeQuery(id+"F36.imprint","IMPRINT",EDGE,{"derivedFrom":sQuery(id+"F36.wireOp",EDGE,"E119.3.0.0")}),-1.0]])]});
            var Q1;
            Q1=sQuery(id+"F36.wireOp",EDGE,"E119.3.0.0");
            revolve(context, id + "F40", {"entities" : qUnion([Q0]), "axis" : qUnion([Q1]), "revolveType" : RevolveType.FULL});
        }
        {
            var Q0;
            Q0=makeQuery(id+"F36.imprint","IMPRINT",FACE,{"disambiguationData":[TD([[makeQuery(id+"F36.imprint","IMPRINT",EDGE,{"derivedFrom":sQuery(id+"F36.wireOp",EDGE,"E119.4.0.0")}),-1.0]])]});
            var Q1;
            Q1=sQuery(id+"F36.wireOp",EDGE,"E119.4.0.0");
            revolve(context, id + "F41", {"entities" : qUnion([Q0]), "axis" : qUnion([Q1]), "revolveType" : RevolveType.FULL});
        }
        {
            var Q0;
            Q0=makeQuery(id+"F36.imprint","IMPRINT",FACE,{"disambiguationData":[TD([[makeQuery(id+"F36.imprint","IMPRINT",EDGE,{"derivedFrom":sQuery(id+"F36.wireOp",EDGE,"E119.5.0.0")}),-1.0]])]});
            var Q1;
            Q1=sQuery(id+"F36.wireOp",EDGE,"E119.5.0.0");
            revolve(context, id + "F42", {"entities" : qUnion([Q0]), "axis" : qUnion([Q1]), "revolveType" : RevolveType.FULL});
        }
        {
            var Q0;
            Q0=makeQuery(id+"F36.imprint","IMPRINT",FACE,{"disambiguationData":[TD([[makeQuery(id+"F36.imprint","IMPRINT",EDGE,{"derivedFrom":sQuery(id+"F36.wireOp",EDGE,"E119.6.0.0")}),-1.0]])]});
            var Q1;
            Q1=sQuery(id+"F36.wireOp",EDGE,"E119.6.0.0");
            revolve(context, id + "F43", {"entities" : qUnion([Q0]), "axis" : qUnion([Q1]), "revolveType" : RevolveType.FULL});
        }
        {
            var Q0;
            Q0=makeQuery(id+"F36.imprint","IMPRINT",FACE,{"disambiguationData":[TD([[makeQuery(id+"F36.imprint","IMPRINT",EDGE,{"derivedFrom":sQuery(id+"F36.wireOp",EDGE,"E119.7.0.0")}),-1.0]])]});
            var Q1;
            Q1=sQuery(id+"F36.wireOp",EDGE,"E119.7.0.0");
            revolve(context, id + "F44", {"entities" : qUnion([Q0]), "axis" : qUnion([Q1]), "revolveType" : RevolveType.FULL});
        }
        {
            var Q0;
            Q0=makeQuery(id+"F36.imprint","IMPRINT",FACE,{"disambiguationData":[TD([[makeQuery(id+"F36.imprint","IMPRINT",EDGE,{"derivedFrom":sQuery(id+"F36.wireOp",EDGE,"E119.8.0.0")}),-1.0]])]});
            var Q1;
            Q1=sQuery(id+"F36.wireOp",EDGE,"E119.8.0.0");
            revolve(context, id + "F45", {"entities" : qUnion([Q0]), "axis" : qUnion([Q1]), "revolveType" : RevolveType.FULL});
        }
        {
            var Q0;
            Q0=makeQuery(id+"F36.imprint","IMPRINT",FACE,{"disambiguationData":[TD([[makeQuery(id+"F36.imprint","IMPRINT",EDGE,{"derivedFrom":sQuery(id+"F36.wireOp",EDGE,"E119.9.0.0")}),-1.0]])]});
            var Q1;
            Q1=sQuery(id+"F36.wireOp",EDGE,"E119.9.0.0");
            revolve(context, id + "F46", {"entities" : qUnion([Q0]), "axis" : qUnion([Q1]), "revolveType" : RevolveType.FULL});
        }
        {
            var Q0;
            Q0=makeQuery(id+"F36.imprint","IMPRINT",FACE,{"disambiguationData":[TD([[makeQuery(id+"F36.imprint","IMPRINT",EDGE,{"derivedFrom":sQuery(id+"F36.wireOp",EDGE,"E119.10.0.0")}),-1.0]])]});
            var Q1;
            Q1=sQuery(id+"F36.wireOp",EDGE,"E119.10.0.0");
            revolve(context, id + "F47", {"entities" : qUnion([Q0]), "axis" : qUnion([Q1]), "revolveType" : RevolveType.FULL});
        }
        {
            var Q0;
            Q0=makeQuery(id+"F36.imprint","IMPRINT",FACE,{"disambiguationData":[TD([[makeQuery(id+"F36.imprint","IMPRINT",EDGE,{"derivedFrom":sQuery(id+"F36.wireOp",EDGE,"E119.11.0.0")}),-1.0]])]});
            var Q1;
            Q1=sQuery(id+"F36.wireOp",EDGE,"E119.11.0.0");
            revolve(context, id + "F48", {"entities" : qUnion([Q0]), "axis" : qUnion([Q1]), "revolveType" : RevolveType.FULL});
        }
        {
            var Q0;
            Q0=qCreatedBy(makeId("Top.planeOp"),FACE);
            var sketch = newSketch(context, id + "F49", { "sketchPlane" : qUnion([Q0])});
            skLineSegment(sketch, "E153", {"start": v(0, 0) * mm, "end": v(0, -10) * mm, "construction": true});
            skLineSegment(sketch, "E154", {"start": v(0, -10) * mm, "end": v(0, -20) * mm, "construction": true});
            skLineSegment(sketch, "E155", {"start": v(0, -20) * mm, "end": v(0, -30) * mm, "construction": true});
            skCircle(sketch, "E156.cCircle", {"center": v(0, -10) * mm, "radius": 1.25 * mm, "construction": true});
            skLineSegment(sketch, "E156.0", {"start": v(-0.72, -8.75) * mm, "end": v(0.72, -8.75) * mm});
            skLineSegment(sketch, "E156.1", {"start": v(0.72, -8.75) * mm, "end": v(1.44, -10) * mm});
            skLineSegment(sketch, "E156.2", {"start": v(1.44, -10) * mm, "end": v(0.72, -11.25) * mm});
            skLineSegment(sketch, "E156.3", {"start": v(0.72, -11.25) * mm, "end": v(-0.72, -11.25) * mm});
            skLineSegment(sketch, "E156.4", {"start": v(-0.72, -11.25) * mm, "end": v(-1.44, -10) * mm});
            skLineSegment(sketch, "E156.5", {"start": v(-1.44, -10) * mm, "end": v(-0.72, -8.75) * mm});
            skPoint(sketch, "E156.0.midPoint", {"position": v(0, -8.75) * mm});
            skCircle(sketch, "E157.cCircle", {"center": v(0, -20) * mm, "radius": 1.5 * mm, "construction": true});
            skLineSegment(sketch, "E157.0", {"start": v(-0.87, -18.5) * mm, "end": v(0.87, -18.5) * mm});
            skLineSegment(sketch, "E157.1", {"start": v(0.87, -18.5) * mm, "end": v(1.73, -20) * mm});
            skLineSegment(sketch, "E157.2", {"start": v(1.73, -20) * mm, "end": v(0.87, -21.5) * mm});
            skLineSegment(sketch, "E157.3", {"start": v(0.87, -21.5) * mm, "end": v(-0.87, -21.5) * mm});
            skLineSegment(sketch, "E157.4", {"start": v(-0.87, -21.5) * mm, "end": v(-1.73, -20) * mm});
            skLineSegment(sketch, "E157.5", {"start": v(-1.73, -20) * mm, "end": v(-0.87, -18.5) * mm});
            skPoint(sketch, "E157.0.midPoint", {"position": v(0, -18.5) * mm});
            skCircle(sketch, "E158.cCircle", {"center": v(0, -30) * mm, "radius": 2 * mm, "construction": true});
            skLineSegment(sketch, "E158.0", {"start": v(-1.15, -28) * mm, "end": v(1.15, -28) * mm});
            skLineSegment(sketch, "E158.1", {"start": v(1.15, -28) * mm, "end": v(2.3, -30) * mm});
            skLineSegment(sketch, "E158.2", {"start": v(2.3, -30) * mm, "end": v(1.15, -32) * mm});
            skLineSegment(sketch, "E158.3", {"start": v(1.15, -32) * mm, "end": v(-1.15, -32) * mm});
            skLineSegment(sketch, "E158.4", {"start": v(-1.15, -32) * mm, "end": v(-2.3, -30) * mm});
            skLineSegment(sketch, "E158.5", {"start": v(-2.3, -30) * mm, "end": v(-1.15, -28) * mm});
            skPoint(sketch, "E158.0.midPoint", {"position": v(0, -28) * mm});
            skPoint(sketch, "E159.1.0.0", {"position": v(10, -8.75) * mm});
            skLineSegment(sketch, "E159.1.0.1", {"start": v(10.72, -11.25) * mm, "end": v(9.28, -11.25) * mm});
            skLineSegment(sketch, "E159.1.0.2", {"start": v(10.87, -21.5) * mm, "end": v(9.13, -21.5) * mm});
            skLineSegment(sketch, "E159.1.0.3", {"start": v(9.13, -18.5) * mm, "end": v(10.87, -18.5) * mm});
            skLineSegment(sketch, "E159.1.0.4", {"start": v(8.56, -10) * mm, "end": v(9.28, -8.75) * mm});
            skLineSegment(sketch, "E159.1.0.5", {"start": v(11.15, -32) * mm, "end": v(8.85, -32) * mm});
            skPoint(sketch, "E159.1.0.6", {"position": v(10, -18.5) * mm});
            skLineSegment(sketch, "E159.1.0.7", {"start": v(8.85, -28) * mm, "end": v(11.15, -28) * mm});
            skPoint(sketch, "E159.1.0.8", {"position": v(10, -28) * mm});
            skLineSegment(sketch, "E159.1.0.9", {"start": v(9.28, -11.25) * mm, "end": v(8.56, -10) * mm});
            skLineSegment(sketch, "E159.1.0.10", {"start": v(9.28, -8.75) * mm, "end": v(10.72, -8.75) * mm});
            skLineSegment(sketch, "E159.1.0.11", {"start": v(8.85, -32) * mm, "end": v(7.7, -30) * mm});
            skLineSegment(sketch, "E159.1.0.12", {"start": v(11.44, -10) * mm, "end": v(10.72, -11.25) * mm});
            skLineSegment(sketch, "E159.1.0.13", {"start": v(12.3, -30) * mm, "end": v(11.15, -32) * mm});
            skLineSegment(sketch, "E159.1.0.14", {"start": v(11.15, -28) * mm, "end": v(12.3, -30) * mm});
            skCircle(sketch, "E159.1.0.15", {"center": v(10, -30) * mm, "radius": 2 * mm, "construction": true});
            skLineSegment(sketch, "E159.1.0.16", {"start": v(11.73, -20) * mm, "end": v(10.87, -21.5) * mm});
            skLineSegment(sketch, "E159.1.0.17", {"start": v(8.27, -20) * mm, "end": v(9.13, -18.5) * mm});
            skLineSegment(sketch, "E159.1.0.18", {"start": v(7.7, -30) * mm, "end": v(8.85, -28) * mm});
            skCircle(sketch, "E159.1.0.19", {"center": v(10, -10) * mm, "radius": 1.25 * mm, "construction": true});
            skLineSegment(sketch, "E159.1.0.20", {"start": v(9.13, -21.5) * mm, "end": v(8.27, -20) * mm});
            skLineSegment(sketch, "E159.1.0.21", {"start": v(10.87, -18.5) * mm, "end": v(11.73, -20) * mm});
            skCircle(sketch, "E159.1.0.22", {"center": v(10, -20) * mm, "radius": 1.5 * mm, "construction": true});
            skLineSegment(sketch, "E159.1.0.23", {"start": v(10.72, -8.75) * mm, "end": v(11.44, -10) * mm});
            skPoint(sketch, "E159.2.0.0", {"position": v(20, -8.75) * mm});
            skLineSegment(sketch, "E159.2.0.1", {"start": v(20.72, -11.25) * mm, "end": v(19.28, -11.25) * mm});
            skLineSegment(sketch, "E159.2.0.2", {"start": v(20.87, -21.5) * mm, "end": v(19.13, -21.5) * mm});
            skLineSegment(sketch, "E159.2.0.3", {"start": v(19.13, -18.5) * mm, "end": v(20.87, -18.5) * mm});
            skLineSegment(sketch, "E159.2.0.4", {"start": v(18.56, -10) * mm, "end": v(19.28, -8.75) * mm});
            skLineSegment(sketch, "E159.2.0.5", {"start": v(21.15, -32) * mm, "end": v(18.85, -32) * mm});
            skPoint(sketch, "E159.2.0.6", {"position": v(20, -18.5) * mm});
            skLineSegment(sketch, "E159.2.0.7", {"start": v(18.85, -28) * mm, "end": v(21.15, -28) * mm});
            skPoint(sketch, "E159.2.0.8", {"position": v(20, -28) * mm});
            skLineSegment(sketch, "E159.2.0.9", {"start": v(19.28, -11.25) * mm, "end": v(18.56, -10) * mm});
            skLineSegment(sketch, "E159.2.0.10", {"start": v(19.28, -8.75) * mm, "end": v(20.72, -8.75) * mm});
            skLineSegment(sketch, "E159.2.0.11", {"start": v(18.85, -32) * mm, "end": v(17.7, -30) * mm});
            skLineSegment(sketch, "E159.2.0.12", {"start": v(21.44, -10) * mm, "end": v(20.72, -11.25) * mm});
            skLineSegment(sketch, "E159.2.0.13", {"start": v(22.3, -30) * mm, "end": v(21.15, -32) * mm});
            skLineSegment(sketch, "E159.2.0.14", {"start": v(21.15, -28) * mm, "end": v(22.3, -30) * mm});
            skCircle(sketch, "E159.2.0.15", {"center": v(20, -30) * mm, "radius": 2 * mm, "construction": true});
            skLineSegment(sketch, "E159.2.0.16", {"start": v(21.73, -20) * mm, "end": v(20.87, -21.5) * mm});
            skLineSegment(sketch, "E159.2.0.17", {"start": v(18.27, -20) * mm, "end": v(19.13, -18.5) * mm});
            skLineSegment(sketch, "E159.2.0.18", {"start": v(17.7, -30) * mm, "end": v(18.85, -28) * mm});
            skCircle(sketch, "E159.2.0.19", {"center": v(20, -10) * mm, "radius": 1.25 * mm, "construction": true});
            skLineSegment(sketch, "E159.2.0.20", {"start": v(19.13, -21.5) * mm, "end": v(18.27, -20) * mm});
            skLineSegment(sketch, "E159.2.0.21", {"start": v(20.87, -18.5) * mm, "end": v(21.73, -20) * mm});
            skCircle(sketch, "E159.2.0.22", {"center": v(20, -20) * mm, "radius": 1.5 * mm, "construction": true});
            skLineSegment(sketch, "E159.2.0.23", {"start": v(20.72, -8.75) * mm, "end": v(21.44, -10) * mm});
            skPoint(sketch, "E159.3.0.0", {"position": v(30, -8.75) * mm});
            skLineSegment(sketch, "E159.3.0.1", {"start": v(30.72, -11.25) * mm, "end": v(29.28, -11.25) * mm});
            skLineSegment(sketch, "E159.3.0.2", {"start": v(30.87, -21.5) * mm, "end": v(29.13, -21.5) * mm});
            skLineSegment(sketch, "E159.3.0.3", {"start": v(29.13, -18.5) * mm, "end": v(30.87, -18.5) * mm});
            skLineSegment(sketch, "E159.3.0.4", {"start": v(28.56, -10) * mm, "end": v(29.28, -8.75) * mm});
            skLineSegment(sketch, "E159.3.0.5", {"start": v(31.15, -32) * mm, "end": v(28.85, -32) * mm});
            skPoint(sketch, "E159.3.0.6", {"position": v(30, -18.5) * mm});
            skLineSegment(sketch, "E159.3.0.7", {"start": v(28.85, -28) * mm, "end": v(31.15, -28) * mm});
            skPoint(sketch, "E159.3.0.8", {"position": v(30, -28) * mm});
            skLineSegment(sketch, "E159.3.0.9", {"start": v(29.28, -11.25) * mm, "end": v(28.56, -10) * mm});
            skLineSegment(sketch, "E159.3.0.10", {"start": v(29.28, -8.75) * mm, "end": v(30.72, -8.75) * mm});
            skLineSegment(sketch, "E159.3.0.11", {"start": v(28.85, -32) * mm, "end": v(27.7, -30) * mm});
            skLineSegment(sketch, "E159.3.0.12", {"start": v(31.44, -10) * mm, "end": v(30.72, -11.25) * mm});
            skLineSegment(sketch, "E159.3.0.13", {"start": v(32.3, -30) * mm, "end": v(31.15, -32) * mm});
            skLineSegment(sketch, "E159.3.0.14", {"start": v(31.15, -28) * mm, "end": v(32.3, -30) * mm});
            skCircle(sketch, "E159.3.0.15", {"center": v(30, -30) * mm, "radius": 2 * mm, "construction": true});
            skLineSegment(sketch, "E159.3.0.16", {"start": v(31.73, -20) * mm, "end": v(30.87, -21.5) * mm});
            skLineSegment(sketch, "E159.3.0.17", {"start": v(28.27, -20) * mm, "end": v(29.13, -18.5) * mm});
            skLineSegment(sketch, "E159.3.0.18", {"start": v(27.7, -30) * mm, "end": v(28.85, -28) * mm});
            skCircle(sketch, "E159.3.0.19", {"center": v(30, -10) * mm, "radius": 1.25 * mm, "construction": true});
            skLineSegment(sketch, "E159.3.0.20", {"start": v(29.13, -21.5) * mm, "end": v(28.27, -20) * mm});
            skLineSegment(sketch, "E159.3.0.21", {"start": v(30.87, -18.5) * mm, "end": v(31.73, -20) * mm});
            skCircle(sketch, "E159.3.0.22", {"center": v(30, -20) * mm, "radius": 1.5 * mm, "construction": true});
            skLineSegment(sketch, "E159.3.0.23", {"start": v(30.72, -8.75) * mm, "end": v(31.44, -10) * mm});
            skPoint(sketch, "E159.4.0.0", {"position": v(40, -8.75) * mm});
            skLineSegment(sketch, "E159.4.0.1", {"start": v(40.72, -11.25) * mm, "end": v(39.28, -11.25) * mm});
            skLineSegment(sketch, "E159.4.0.2", {"start": v(40.87, -21.5) * mm, "end": v(39.13, -21.5) * mm});
            skLineSegment(sketch, "E159.4.0.3", {"start": v(39.13, -18.5) * mm, "end": v(40.87, -18.5) * mm});
            skLineSegment(sketch, "E159.4.0.4", {"start": v(38.56, -10) * mm, "end": v(39.28, -8.75) * mm});
            skLineSegment(sketch, "E159.4.0.5", {"start": v(41.15, -32) * mm, "end": v(38.85, -32) * mm});
            skPoint(sketch, "E159.4.0.6", {"position": v(40, -18.5) * mm});
            skLineSegment(sketch, "E159.4.0.7", {"start": v(38.85, -28) * mm, "end": v(41.15, -28) * mm});
            skPoint(sketch, "E159.4.0.8", {"position": v(40, -28) * mm});
            skLineSegment(sketch, "E159.4.0.9", {"start": v(39.28, -11.25) * mm, "end": v(38.56, -10) * mm});
            skLineSegment(sketch, "E159.4.0.10", {"start": v(39.28, -8.75) * mm, "end": v(40.72, -8.75) * mm});
            skLineSegment(sketch, "E159.4.0.11", {"start": v(38.85, -32) * mm, "end": v(37.7, -30) * mm});
            skLineSegment(sketch, "E159.4.0.12", {"start": v(41.44, -10) * mm, "end": v(40.72, -11.25) * mm});
            skLineSegment(sketch, "E159.4.0.13", {"start": v(42.3, -30) * mm, "end": v(41.15, -32) * mm});
            skLineSegment(sketch, "E159.4.0.14", {"start": v(41.15, -28) * mm, "end": v(42.3, -30) * mm});
            skCircle(sketch, "E159.4.0.15", {"center": v(40, -30) * mm, "radius": 2 * mm, "construction": true});
            skLineSegment(sketch, "E159.4.0.16", {"start": v(41.73, -20) * mm, "end": v(40.87, -21.5) * mm});
            skLineSegment(sketch, "E159.4.0.17", {"start": v(38.27, -20) * mm, "end": v(39.13, -18.5) * mm});
            skLineSegment(sketch, "E159.4.0.18", {"start": v(37.7, -30) * mm, "end": v(38.85, -28) * mm});
            skCircle(sketch, "E159.4.0.19", {"center": v(40, -10) * mm, "radius": 1.25 * mm, "construction": true});
            skLineSegment(sketch, "E159.4.0.20", {"start": v(39.13, -21.5) * mm, "end": v(38.27, -20) * mm});
            skLineSegment(sketch, "E159.4.0.21", {"start": v(40.87, -18.5) * mm, "end": v(41.73, -20) * mm});
            skCircle(sketch, "E159.4.0.22", {"center": v(40, -20) * mm, "radius": 1.5 * mm, "construction": true});
            skLineSegment(sketch, "E159.4.0.23", {"start": v(40.72, -8.75) * mm, "end": v(41.44, -10) * mm});
            skPoint(sketch, "E159.5.0.0", {"position": v(50, -8.75) * mm});
            skLineSegment(sketch, "E159.5.0.1", {"start": v(50.72, -11.25) * mm, "end": v(49.28, -11.25) * mm});
            skLineSegment(sketch, "E159.5.0.2", {"start": v(50.87, -21.5) * mm, "end": v(49.13, -21.5) * mm});
            skLineSegment(sketch, "E159.5.0.3", {"start": v(49.13, -18.5) * mm, "end": v(50.87, -18.5) * mm});
            skLineSegment(sketch, "E159.5.0.4", {"start": v(48.56, -10) * mm, "end": v(49.28, -8.75) * mm});
            skLineSegment(sketch, "E159.5.0.5", {"start": v(51.15, -32) * mm, "end": v(48.85, -32) * mm});
            skPoint(sketch, "E159.5.0.6", {"position": v(50, -18.5) * mm});
            skLineSegment(sketch, "E159.5.0.7", {"start": v(48.85, -28) * mm, "end": v(51.15, -28) * mm});
            skPoint(sketch, "E159.5.0.8", {"position": v(50, -28) * mm});
            skLineSegment(sketch, "E159.5.0.9", {"start": v(49.28, -11.25) * mm, "end": v(48.56, -10) * mm});
            skLineSegment(sketch, "E159.5.0.10", {"start": v(49.28, -8.75) * mm, "end": v(50.72, -8.75) * mm});
            skLineSegment(sketch, "E159.5.0.11", {"start": v(48.85, -32) * mm, "end": v(47.7, -30) * mm});
            skLineSegment(sketch, "E159.5.0.12", {"start": v(51.44, -10) * mm, "end": v(50.72, -11.25) * mm});
            skLineSegment(sketch, "E159.5.0.13", {"start": v(52.3, -30) * mm, "end": v(51.15, -32) * mm});
            skLineSegment(sketch, "E159.5.0.14", {"start": v(51.15, -28) * mm, "end": v(52.3, -30) * mm});
            skCircle(sketch, "E159.5.0.15", {"center": v(50, -30) * mm, "radius": 2 * mm, "construction": true});
            skLineSegment(sketch, "E159.5.0.16", {"start": v(51.73, -20) * mm, "end": v(50.87, -21.5) * mm});
            skLineSegment(sketch, "E159.5.0.17", {"start": v(48.27, -20) * mm, "end": v(49.13, -18.5) * mm});
            skLineSegment(sketch, "E159.5.0.18", {"start": v(47.7, -30) * mm, "end": v(48.85, -28) * mm});
            skCircle(sketch, "E159.5.0.19", {"center": v(50, -10) * mm, "radius": 1.25 * mm, "construction": true});
            skLineSegment(sketch, "E159.5.0.20", {"start": v(49.13, -21.5) * mm, "end": v(48.27, -20) * mm});
            skLineSegment(sketch, "E159.5.0.21", {"start": v(50.87, -18.5) * mm, "end": v(51.73, -20) * mm});
            skCircle(sketch, "E159.5.0.22", {"center": v(50, -20) * mm, "radius": 1.5 * mm, "construction": true});
            skLineSegment(sketch, "E159.5.0.23", {"start": v(50.72, -8.75) * mm, "end": v(51.44, -10) * mm});
            skPoint(sketch, "E159.6.0.0", {"position": v(60, -8.75) * mm});
            skLineSegment(sketch, "E159.6.0.1", {"start": v(60.72, -11.25) * mm, "end": v(59.28, -11.25) * mm});
            skLineSegment(sketch, "E159.6.0.2", {"start": v(60.87, -21.5) * mm, "end": v(59.13, -21.5) * mm});
            skLineSegment(sketch, "E159.6.0.3", {"start": v(59.13, -18.5) * mm, "end": v(60.87, -18.5) * mm});
            skLineSegment(sketch, "E159.6.0.4", {"start": v(58.56, -10) * mm, "end": v(59.28, -8.75) * mm});
            skLineSegment(sketch, "E159.6.0.5", {"start": v(61.15, -32) * mm, "end": v(58.85, -32) * mm});
            skPoint(sketch, "E159.6.0.6", {"position": v(60, -18.5) * mm});
            skLineSegment(sketch, "E159.6.0.7", {"start": v(58.85, -28) * mm, "end": v(61.15, -28) * mm});
            skPoint(sketch, "E159.6.0.8", {"position": v(60, -28) * mm});
            skLineSegment(sketch, "E159.6.0.9", {"start": v(59.28, -11.25) * mm, "end": v(58.56, -10) * mm});
            skLineSegment(sketch, "E159.6.0.10", {"start": v(59.28, -8.75) * mm, "end": v(60.72, -8.75) * mm});
            skLineSegment(sketch, "E159.6.0.11", {"start": v(58.85, -32) * mm, "end": v(57.7, -30) * mm});
            skLineSegment(sketch, "E159.6.0.12", {"start": v(61.44, -10) * mm, "end": v(60.72, -11.25) * mm});
            skLineSegment(sketch, "E159.6.0.13", {"start": v(62.3, -30) * mm, "end": v(61.15, -32) * mm});
            skLineSegment(sketch, "E159.6.0.14", {"start": v(61.15, -28) * mm, "end": v(62.3, -30) * mm});
            skCircle(sketch, "E159.6.0.15", {"center": v(60, -30) * mm, "radius": 2 * mm, "construction": true});
            skLineSegment(sketch, "E159.6.0.16", {"start": v(61.73, -20) * mm, "end": v(60.87, -21.5) * mm});
            skLineSegment(sketch, "E159.6.0.17", {"start": v(58.27, -20) * mm, "end": v(59.13, -18.5) * mm});
            skLineSegment(sketch, "E159.6.0.18", {"start": v(57.7, -30) * mm, "end": v(58.85, -28) * mm});
            skCircle(sketch, "E159.6.0.19", {"center": v(60, -10) * mm, "radius": 1.25 * mm, "construction": true});
            skLineSegment(sketch, "E159.6.0.20", {"start": v(59.13, -21.5) * mm, "end": v(58.27, -20) * mm});
            skLineSegment(sketch, "E159.6.0.21", {"start": v(60.87, -18.5) * mm, "end": v(61.73, -20) * mm});
            skCircle(sketch, "E159.6.0.22", {"center": v(60, -20) * mm, "radius": 1.5 * mm, "construction": true});
            skLineSegment(sketch, "E159.6.0.23", {"start": v(60.72, -8.75) * mm, "end": v(61.44, -10) * mm});
            skPoint(sketch, "E159.7.0.0", {"position": v(70, -8.75) * mm});
            skLineSegment(sketch, "E159.7.0.1", {"start": v(70.72, -11.25) * mm, "end": v(69.28, -11.25) * mm});
            skLineSegment(sketch, "E159.7.0.2", {"start": v(70.87, -21.5) * mm, "end": v(69.13, -21.5) * mm});
            skLineSegment(sketch, "E159.7.0.3", {"start": v(69.13, -18.5) * mm, "end": v(70.87, -18.5) * mm});
            skLineSegment(sketch, "E159.7.0.4", {"start": v(68.56, -10) * mm, "end": v(69.28, -8.75) * mm});
            skLineSegment(sketch, "E159.7.0.5", {"start": v(71.15, -32) * mm, "end": v(68.85, -32) * mm});
            skPoint(sketch, "E159.7.0.6", {"position": v(70, -18.5) * mm});
            skLineSegment(sketch, "E159.7.0.7", {"start": v(68.85, -28) * mm, "end": v(71.15, -28) * mm});
            skPoint(sketch, "E159.7.0.8", {"position": v(70, -28) * mm});
            skLineSegment(sketch, "E159.7.0.9", {"start": v(69.28, -11.25) * mm, "end": v(68.56, -10) * mm});
            skLineSegment(sketch, "E159.7.0.10", {"start": v(69.28, -8.75) * mm, "end": v(70.72, -8.75) * mm});
            skLineSegment(sketch, "E159.7.0.11", {"start": v(68.85, -32) * mm, "end": v(67.7, -30) * mm});
            skLineSegment(sketch, "E159.7.0.12", {"start": v(71.44, -10) * mm, "end": v(70.72, -11.25) * mm});
            skLineSegment(sketch, "E159.7.0.13", {"start": v(72.3, -30) * mm, "end": v(71.15, -32) * mm});
            skLineSegment(sketch, "E159.7.0.14", {"start": v(71.15, -28) * mm, "end": v(72.3, -30) * mm});
            skCircle(sketch, "E159.7.0.15", {"center": v(70, -30) * mm, "radius": 2 * mm, "construction": true});
            skLineSegment(sketch, "E159.7.0.16", {"start": v(71.73, -20) * mm, "end": v(70.87, -21.5) * mm});
            skLineSegment(sketch, "E159.7.0.17", {"start": v(68.27, -20) * mm, "end": v(69.13, -18.5) * mm});
            skLineSegment(sketch, "E159.7.0.18", {"start": v(67.7, -30) * mm, "end": v(68.85, -28) * mm});
            skCircle(sketch, "E159.7.0.19", {"center": v(70, -10) * mm, "radius": 1.25 * mm, "construction": true});
            skLineSegment(sketch, "E159.7.0.20", {"start": v(69.13, -21.5) * mm, "end": v(68.27, -20) * mm});
            skLineSegment(sketch, "E159.7.0.21", {"start": v(70.87, -18.5) * mm, "end": v(71.73, -20) * mm});
            skCircle(sketch, "E159.7.0.22", {"center": v(70, -20) * mm, "radius": 1.5 * mm, "construction": true});
            skLineSegment(sketch, "E159.7.0.23", {"start": v(70.72, -8.75) * mm, "end": v(71.44, -10) * mm});
            skPoint(sketch, "E159.8.0.0", {"position": v(80, -8.75) * mm});
            skLineSegment(sketch, "E159.8.0.1", {"start": v(80.72, -11.25) * mm, "end": v(79.28, -11.25) * mm});
            skLineSegment(sketch, "E159.8.0.2", {"start": v(80.87, -21.5) * mm, "end": v(79.13, -21.5) * mm});
            skLineSegment(sketch, "E159.8.0.3", {"start": v(79.13, -18.5) * mm, "end": v(80.87, -18.5) * mm});
            skLineSegment(sketch, "E159.8.0.4", {"start": v(78.56, -10) * mm, "end": v(79.28, -8.75) * mm});
            skLineSegment(sketch, "E159.8.0.5", {"start": v(81.15, -32) * mm, "end": v(78.85, -32) * mm});
            skPoint(sketch, "E159.8.0.6", {"position": v(80, -18.5) * mm});
            skLineSegment(sketch, "E159.8.0.7", {"start": v(78.85, -28) * mm, "end": v(81.15, -28) * mm});
            skPoint(sketch, "E159.8.0.8", {"position": v(80, -28) * mm});
            skLineSegment(sketch, "E159.8.0.9", {"start": v(79.28, -11.25) * mm, "end": v(78.56, -10) * mm});
            skLineSegment(sketch, "E159.8.0.10", {"start": v(79.28, -8.75) * mm, "end": v(80.72, -8.75) * mm});
            skLineSegment(sketch, "E159.8.0.11", {"start": v(78.85, -32) * mm, "end": v(77.7, -30) * mm});
            skLineSegment(sketch, "E159.8.0.12", {"start": v(81.44, -10) * mm, "end": v(80.72, -11.25) * mm});
            skLineSegment(sketch, "E159.8.0.13", {"start": v(82.3, -30) * mm, "end": v(81.15, -32) * mm});
            skLineSegment(sketch, "E159.8.0.14", {"start": v(81.15, -28) * mm, "end": v(82.3, -30) * mm});
            skCircle(sketch, "E159.8.0.15", {"center": v(80, -30) * mm, "radius": 2 * mm, "construction": true});
            skLineSegment(sketch, "E159.8.0.16", {"start": v(81.73, -20) * mm, "end": v(80.87, -21.5) * mm});
            skLineSegment(sketch, "E159.8.0.17", {"start": v(78.27, -20) * mm, "end": v(79.13, -18.5) * mm});
            skLineSegment(sketch, "E159.8.0.18", {"start": v(77.7, -30) * mm, "end": v(78.85, -28) * mm});
            skCircle(sketch, "E159.8.0.19", {"center": v(80, -10) * mm, "radius": 1.25 * mm, "construction": true});
            skLineSegment(sketch, "E159.8.0.20", {"start": v(79.13, -21.5) * mm, "end": v(78.27, -20) * mm});
            skLineSegment(sketch, "E159.8.0.21", {"start": v(80.87, -18.5) * mm, "end": v(81.73, -20) * mm});
            skCircle(sketch, "E159.8.0.22", {"center": v(80, -20) * mm, "radius": 1.5 * mm, "construction": true});
            skLineSegment(sketch, "E159.8.0.23", {"start": v(80.72, -8.75) * mm, "end": v(81.44, -10) * mm});
            skPoint(sketch, "E159.9.0.0", {"position": v(90, -8.75) * mm});
            skLineSegment(sketch, "E159.9.0.1", {"start": v(90.72, -11.25) * mm, "end": v(89.28, -11.25) * mm});
            skLineSegment(sketch, "E159.9.0.2", {"start": v(90.87, -21.5) * mm, "end": v(89.13, -21.5) * mm});
            skLineSegment(sketch, "E159.9.0.3", {"start": v(89.13, -18.5) * mm, "end": v(90.87, -18.5) * mm});
            skLineSegment(sketch, "E159.9.0.4", {"start": v(88.56, -10) * mm, "end": v(89.28, -8.75) * mm});
            skLineSegment(sketch, "E159.9.0.5", {"start": v(91.15, -32) * mm, "end": v(88.85, -32) * mm});
            skPoint(sketch, "E159.9.0.6", {"position": v(90, -18.5) * mm});
            skLineSegment(sketch, "E159.9.0.7", {"start": v(88.85, -28) * mm, "end": v(91.15, -28) * mm});
            skPoint(sketch, "E159.9.0.8", {"position": v(90, -28) * mm});
            skLineSegment(sketch, "E159.9.0.9", {"start": v(89.28, -11.25) * mm, "end": v(88.56, -10) * mm});
            skLineSegment(sketch, "E159.9.0.10", {"start": v(89.28, -8.75) * mm, "end": v(90.72, -8.75) * mm});
            skLineSegment(sketch, "E159.9.0.11", {"start": v(88.85, -32) * mm, "end": v(87.7, -30) * mm});
            skLineSegment(sketch, "E159.9.0.12", {"start": v(91.44, -10) * mm, "end": v(90.72, -11.25) * mm});
            skLineSegment(sketch, "E159.9.0.13", {"start": v(92.3, -30) * mm, "end": v(91.15, -32) * mm});
            skLineSegment(sketch, "E159.9.0.14", {"start": v(91.15, -28) * mm, "end": v(92.3, -30) * mm});
            skCircle(sketch, "E159.9.0.15", {"center": v(90, -30) * mm, "radius": 2 * mm, "construction": true});
            skLineSegment(sketch, "E159.9.0.16", {"start": v(91.73, -20) * mm, "end": v(90.87, -21.5) * mm});
            skLineSegment(sketch, "E159.9.0.17", {"start": v(88.27, -20) * mm, "end": v(89.13, -18.5) * mm});
            skLineSegment(sketch, "E159.9.0.18", {"start": v(87.7, -30) * mm, "end": v(88.85, -28) * mm});
            skCircle(sketch, "E159.9.0.19", {"center": v(90, -10) * mm, "radius": 1.25 * mm, "construction": true});
            skLineSegment(sketch, "E159.9.0.20", {"start": v(89.13, -21.5) * mm, "end": v(88.27, -20) * mm});
            skLineSegment(sketch, "E159.9.0.21", {"start": v(90.87, -18.5) * mm, "end": v(91.73, -20) * mm});
            skCircle(sketch, "E159.9.0.22", {"center": v(90, -20) * mm, "radius": 1.5 * mm, "construction": true});
            skLineSegment(sketch, "E159.9.0.23", {"start": v(90.72, -8.75) * mm, "end": v(91.44, -10) * mm});
            skPoint(sketch, "E159.10.0.0", {"position": v(100, -8.75) * mm});
            skLineSegment(sketch, "E159.10.0.1", {"start": v(100.72, -11.25) * mm, "end": v(99.28, -11.25) * mm});
            skLineSegment(sketch, "E159.10.0.2", {"start": v(100.87, -21.5) * mm, "end": v(99.13, -21.5) * mm});
            skLineSegment(sketch, "E159.10.0.3", {"start": v(99.13, -18.5) * mm, "end": v(100.87, -18.5) * mm});
            skLineSegment(sketch, "E159.10.0.4", {"start": v(98.56, -10) * mm, "end": v(99.28, -8.75) * mm});
            skLineSegment(sketch, "E159.10.0.5", {"start": v(101.15, -32) * mm, "end": v(98.85, -32) * mm});
            skPoint(sketch, "E159.10.0.6", {"position": v(100, -18.5) * mm});
            skLineSegment(sketch, "E159.10.0.7", {"start": v(98.85, -28) * mm, "end": v(101.15, -28) * mm});
            skPoint(sketch, "E159.10.0.8", {"position": v(100, -28) * mm});
            skLineSegment(sketch, "E159.10.0.9", {"start": v(99.28, -11.25) * mm, "end": v(98.56, -10) * mm});
            skLineSegment(sketch, "E159.10.0.10", {"start": v(99.28, -8.75) * mm, "end": v(100.72, -8.75) * mm});
            skLineSegment(sketch, "E159.10.0.11", {"start": v(98.85, -32) * mm, "end": v(97.7, -30) * mm});
            skLineSegment(sketch, "E159.10.0.12", {"start": v(101.44, -10) * mm, "end": v(100.72, -11.25) * mm});
            skLineSegment(sketch, "E159.10.0.13", {"start": v(102.3, -30) * mm, "end": v(101.15, -32) * mm});
            skLineSegment(sketch, "E159.10.0.14", {"start": v(101.15, -28) * mm, "end": v(102.3, -30) * mm});
            skCircle(sketch, "E159.10.0.15", {"center": v(100, -30) * mm, "radius": 2 * mm, "construction": true});
            skLineSegment(sketch, "E159.10.0.16", {"start": v(101.73, -20) * mm, "end": v(100.87, -21.5) * mm});
            skLineSegment(sketch, "E159.10.0.17", {"start": v(98.27, -20) * mm, "end": v(99.13, -18.5) * mm});
            skLineSegment(sketch, "E159.10.0.18", {"start": v(97.7, -30) * mm, "end": v(98.85, -28) * mm});
            skCircle(sketch, "E159.10.0.19", {"center": v(100, -10) * mm, "radius": 1.25 * mm, "construction": true});
            skLineSegment(sketch, "E159.10.0.20", {"start": v(99.13, -21.5) * mm, "end": v(98.27, -20) * mm});
            skLineSegment(sketch, "E159.10.0.21", {"start": v(100.87, -18.5) * mm, "end": v(101.73, -20) * mm});
            skCircle(sketch, "E159.10.0.22", {"center": v(100, -20) * mm, "radius": 1.5 * mm, "construction": true});
            skLineSegment(sketch, "E159.10.0.23", {"start": v(100.72, -8.75) * mm, "end": v(101.44, -10) * mm});
            skPoint(sketch, "E159.11.0.0", {"position": v(110, -8.75) * mm});
            skLineSegment(sketch, "E159.11.0.1", {"start": v(110.72, -11.25) * mm, "end": v(109.28, -11.25) * mm});
            skLineSegment(sketch, "E159.11.0.2", {"start": v(110.87, -21.5) * mm, "end": v(109.13, -21.5) * mm});
            skLineSegment(sketch, "E159.11.0.3", {"start": v(109.13, -18.5) * mm, "end": v(110.87, -18.5) * mm});
            skLineSegment(sketch, "E159.11.0.4", {"start": v(108.56, -10) * mm, "end": v(109.28, -8.75) * mm});
            skLineSegment(sketch, "E159.11.0.5", {"start": v(111.15, -32) * mm, "end": v(108.85, -32) * mm});
            skPoint(sketch, "E159.11.0.6", {"position": v(110, -18.5) * mm});
            skLineSegment(sketch, "E159.11.0.7", {"start": v(108.85, -28) * mm, "end": v(111.15, -28) * mm});
            skPoint(sketch, "E159.11.0.8", {"position": v(110, -28) * mm});
            skLineSegment(sketch, "E159.11.0.9", {"start": v(109.28, -11.25) * mm, "end": v(108.56, -10) * mm});
            skLineSegment(sketch, "E159.11.0.10", {"start": v(109.28, -8.75) * mm, "end": v(110.72, -8.75) * mm});
            skLineSegment(sketch, "E159.11.0.11", {"start": v(108.85, -32) * mm, "end": v(107.7, -30) * mm});
            skLineSegment(sketch, "E159.11.0.12", {"start": v(111.44, -10) * mm, "end": v(110.72, -11.25) * mm});
            skLineSegment(sketch, "E159.11.0.13", {"start": v(112.3, -30) * mm, "end": v(111.15, -32) * mm});
            skLineSegment(sketch, "E159.11.0.14", {"start": v(111.15, -28) * mm, "end": v(112.3, -30) * mm});
            skCircle(sketch, "E159.11.0.15", {"center": v(110, -30) * mm, "radius": 2 * mm, "construction": true});
            skLineSegment(sketch, "E159.11.0.16", {"start": v(111.73, -20) * mm, "end": v(110.87, -21.5) * mm});
            skLineSegment(sketch, "E159.11.0.17", {"start": v(108.27, -20) * mm, "end": v(109.13, -18.5) * mm});
            skLineSegment(sketch, "E159.11.0.18", {"start": v(107.7, -30) * mm, "end": v(108.85, -28) * mm});
            skCircle(sketch, "E159.11.0.19", {"center": v(110, -10) * mm, "radius": 1.25 * mm, "construction": true});
            skLineSegment(sketch, "E159.11.0.20", {"start": v(109.13, -21.5) * mm, "end": v(108.27, -20) * mm});
            skLineSegment(sketch, "E159.11.0.21", {"start": v(110.87, -18.5) * mm, "end": v(111.73, -20) * mm});
            skCircle(sketch, "E159.11.0.22", {"center": v(110, -20) * mm, "radius": 1.5 * mm, "construction": true});
            skLineSegment(sketch, "E159.11.0.23", {"start": v(110.72, -8.75) * mm, "end": v(111.44, -10) * mm});
            skPoint(sketch, "E159.12.0.0", {"position": v(120, -8.75) * mm});
            skLineSegment(sketch, "E159.12.0.1", {"start": v(120.72, -11.25) * mm, "end": v(119.28, -11.25) * mm});
            skLineSegment(sketch, "E159.12.0.2", {"start": v(120.87, -21.5) * mm, "end": v(119.13, -21.5) * mm});
            skLineSegment(sketch, "E159.12.0.3", {"start": v(119.13, -18.5) * mm, "end": v(120.87, -18.5) * mm});
            skLineSegment(sketch, "E159.12.0.4", {"start": v(118.56, -10) * mm, "end": v(119.28, -8.75) * mm});
            skLineSegment(sketch, "E159.12.0.5", {"start": v(121.15, -32) * mm, "end": v(118.85, -32) * mm});
            skPoint(sketch, "E159.12.0.6", {"position": v(120, -18.5) * mm});
            skLineSegment(sketch, "E159.12.0.7", {"start": v(118.85, -28) * mm, "end": v(121.15, -28) * mm});
            skPoint(sketch, "E159.12.0.8", {"position": v(120, -28) * mm});
            skLineSegment(sketch, "E159.12.0.9", {"start": v(119.28, -11.25) * mm, "end": v(118.56, -10) * mm});
            skLineSegment(sketch, "E159.12.0.10", {"start": v(119.28, -8.75) * mm, "end": v(120.72, -8.75) * mm});
            skLineSegment(sketch, "E159.12.0.11", {"start": v(118.85, -32) * mm, "end": v(117.7, -30) * mm});
            skLineSegment(sketch, "E159.12.0.12", {"start": v(121.44, -10) * mm, "end": v(120.72, -11.25) * mm});
            skLineSegment(sketch, "E159.12.0.13", {"start": v(122.3, -30) * mm, "end": v(121.15, -32) * mm});
            skLineSegment(sketch, "E159.12.0.14", {"start": v(121.15, -28) * mm, "end": v(122.3, -30) * mm});
            skCircle(sketch, "E159.12.0.15", {"center": v(120, -30) * mm, "radius": 2 * mm, "construction": true});
            skLineSegment(sketch, "E159.12.0.16", {"start": v(121.73, -20) * mm, "end": v(120.87, -21.5) * mm});
            skLineSegment(sketch, "E159.12.0.17", {"start": v(118.27, -20) * mm, "end": v(119.13, -18.5) * mm});
            skLineSegment(sketch, "E159.12.0.18", {"start": v(117.7, -30) * mm, "end": v(118.85, -28) * mm});
            skCircle(sketch, "E159.12.0.19", {"center": v(120, -10) * mm, "radius": 1.25 * mm, "construction": true});
            skLineSegment(sketch, "E159.12.0.20", {"start": v(119.13, -21.5) * mm, "end": v(118.27, -20) * mm});
            skLineSegment(sketch, "E159.12.0.21", {"start": v(120.87, -18.5) * mm, "end": v(121.73, -20) * mm});
            skCircle(sketch, "E159.12.0.22", {"center": v(120, -20) * mm, "radius": 1.5 * mm, "construction": true});
            skLineSegment(sketch, "E159.12.0.23", {"start": v(120.72, -8.75) * mm, "end": v(121.44, -10) * mm});
            skPoint(sketch, "E159.13.0.0", {"position": v(130, -8.75) * mm});
            skLineSegment(sketch, "E159.13.0.1", {"start": v(130.72, -11.25) * mm, "end": v(129.28, -11.25) * mm});
            skLineSegment(sketch, "E159.13.0.2", {"start": v(130.87, -21.5) * mm, "end": v(129.13, -21.5) * mm});
            skLineSegment(sketch, "E159.13.0.3", {"start": v(129.13, -18.5) * mm, "end": v(130.87, -18.5) * mm});
            skLineSegment(sketch, "E159.13.0.4", {"start": v(128.56, -10) * mm, "end": v(129.28, -8.75) * mm});
            skLineSegment(sketch, "E159.13.0.5", {"start": v(131.15, -32) * mm, "end": v(128.85, -32) * mm});
            skPoint(sketch, "E159.13.0.6", {"position": v(130, -18.5) * mm});
            skLineSegment(sketch, "E159.13.0.7", {"start": v(128.85, -28) * mm, "end": v(131.15, -28) * mm});
            skPoint(sketch, "E159.13.0.8", {"position": v(130, -28) * mm});
            skLineSegment(sketch, "E159.13.0.9", {"start": v(129.28, -11.25) * mm, "end": v(128.56, -10) * mm});
            skLineSegment(sketch, "E159.13.0.10", {"start": v(129.28, -8.75) * mm, "end": v(130.72, -8.75) * mm});
            skLineSegment(sketch, "E159.13.0.11", {"start": v(128.85, -32) * mm, "end": v(127.7, -30) * mm});
            skLineSegment(sketch, "E159.13.0.12", {"start": v(131.44, -10) * mm, "end": v(130.72, -11.25) * mm});
            skLineSegment(sketch, "E159.13.0.13", {"start": v(132.3, -30) * mm, "end": v(131.15, -32) * mm});
            skLineSegment(sketch, "E159.13.0.14", {"start": v(131.15, -28) * mm, "end": v(132.3, -30) * mm});
            skCircle(sketch, "E159.13.0.15", {"center": v(130, -30) * mm, "radius": 2 * mm, "construction": true});
            skLineSegment(sketch, "E159.13.0.16", {"start": v(131.73, -20) * mm, "end": v(130.87, -21.5) * mm});
            skLineSegment(sketch, "E159.13.0.17", {"start": v(128.27, -20) * mm, "end": v(129.13, -18.5) * mm});
            skLineSegment(sketch, "E159.13.0.18", {"start": v(127.7, -30) * mm, "end": v(128.85, -28) * mm});
            skCircle(sketch, "E159.13.0.19", {"center": v(130, -10) * mm, "radius": 1.25 * mm, "construction": true});
            skLineSegment(sketch, "E159.13.0.20", {"start": v(129.13, -21.5) * mm, "end": v(128.27, -20) * mm});
            skLineSegment(sketch, "E159.13.0.21", {"start": v(130.87, -18.5) * mm, "end": v(131.73, -20) * mm});
            skCircle(sketch, "E159.13.0.22", {"center": v(130, -20) * mm, "radius": 1.5 * mm, "construction": true});
            skLineSegment(sketch, "E159.13.0.23", {"start": v(130.72, -8.75) * mm, "end": v(131.44, -10) * mm});
            skLineSegment(sketch, "E159.direction1", {"start": v(0, -8.75) * mm, "end": v(10, -8.75) * mm, "construction": true});
            skPoint(sketch, "E160.0.14.0", {"position": v(140, -8.75) * mm});
            skLineSegment(sketch, "E160.1.14.0", {"start": v(140.72, -11.25) * mm, "end": v(139.28, -11.25) * mm});
            skLineSegment(sketch, "E160.4.14.0", {"start": v(140.87, -21.5) * mm, "end": v(139.13, -21.5) * mm});
            skLineSegment(sketch, "E160.7.14.0", {"start": v(139.13, -18.5) * mm, "end": v(140.87, -18.5) * mm});
            skLineSegment(sketch, "E160.10.14.0", {"start": v(138.56, -10) * mm, "end": v(139.28, -8.75) * mm});
            skLineSegment(sketch, "E160.13.14.0", {"start": v(141.15, -32) * mm, "end": v(138.85, -32) * mm});
            skPoint(sketch, "E160.16.14.0", {"position": v(140, -18.5) * mm});
            skLineSegment(sketch, "E160.17.14.0", {"start": v(138.85, -28) * mm, "end": v(141.15, -28) * mm});
            skPoint(sketch, "E160.20.14.0", {"position": v(140, -28) * mm});
            skLineSegment(sketch, "E160.21.14.0", {"start": v(139.28, -11.25) * mm, "end": v(138.56, -10) * mm});
            skLineSegment(sketch, "E160.24.14.0", {"start": v(139.28, -8.75) * mm, "end": v(140.72, -8.75) * mm});
            skLineSegment(sketch, "E160.27.14.0", {"start": v(138.85, -32) * mm, "end": v(137.7, -30) * mm});
            skLineSegment(sketch, "E160.30.14.0", {"start": v(141.44, -10) * mm, "end": v(140.72, -11.25) * mm});
            skLineSegment(sketch, "E160.33.14.0", {"start": v(142.3, -30) * mm, "end": v(141.15, -32) * mm});
            skLineSegment(sketch, "E160.36.14.0", {"start": v(141.15, -28) * mm, "end": v(142.3, -30) * mm});
            skCircle(sketch, "E160.39.14.0", {"center": v(140, -30) * mm, "radius": 2 * mm, "construction": true});
            skLineSegment(sketch, "E160.41.14.0", {"start": v(141.73, -20) * mm, "end": v(140.87, -21.5) * mm});
            skLineSegment(sketch, "E160.44.14.0", {"start": v(138.27, -20) * mm, "end": v(139.13, -18.5) * mm});
            skLineSegment(sketch, "E160.47.14.0", {"start": v(137.7, -30) * mm, "end": v(138.85, -28) * mm});
            skCircle(sketch, "E160.50.14.0", {"center": v(140, -10) * mm, "radius": 1.25 * mm, "construction": true});
            skLineSegment(sketch, "E160.52.14.0", {"start": v(139.13, -21.5) * mm, "end": v(138.27, -20) * mm});
            skLineSegment(sketch, "E160.55.14.0", {"start": v(140.87, -18.5) * mm, "end": v(141.73, -20) * mm});
            skCircle(sketch, "E160.58.14.0", {"center": v(140, -20) * mm, "radius": 1.5 * mm, "construction": true});
            skLineSegment(sketch, "E160.60.14.0", {"start": v(140.72, -8.75) * mm, "end": v(141.44, -10) * mm});
            skPoint(sketch, "E160.0.15.0", {"position": v(150, -8.75) * mm});
            skLineSegment(sketch, "E160.1.15.0", {"start": v(150.72, -11.25) * mm, "end": v(149.28, -11.25) * mm});
            skLineSegment(sketch, "E160.4.15.0", {"start": v(150.87, -21.5) * mm, "end": v(149.13, -21.5) * mm});
            skLineSegment(sketch, "E160.7.15.0", {"start": v(149.13, -18.5) * mm, "end": v(150.87, -18.5) * mm});
            skLineSegment(sketch, "E160.10.15.0", {"start": v(148.56, -10) * mm, "end": v(149.28, -8.75) * mm});
            skLineSegment(sketch, "E160.13.15.0", {"start": v(151.15, -32) * mm, "end": v(148.85, -32) * mm});
            skPoint(sketch, "E160.16.15.0", {"position": v(150, -18.5) * mm});
            skLineSegment(sketch, "E160.17.15.0", {"start": v(148.85, -28) * mm, "end": v(151.15, -28) * mm});
            skPoint(sketch, "E160.20.15.0", {"position": v(150, -28) * mm});
            skLineSegment(sketch, "E160.21.15.0", {"start": v(149.28, -11.25) * mm, "end": v(148.56, -10) * mm});
            skLineSegment(sketch, "E160.24.15.0", {"start": v(149.28, -8.75) * mm, "end": v(150.72, -8.75) * mm});
            skLineSegment(sketch, "E160.27.15.0", {"start": v(148.85, -32) * mm, "end": v(147.7, -30) * mm});
            skLineSegment(sketch, "E160.30.15.0", {"start": v(151.44, -10) * mm, "end": v(150.72, -11.25) * mm});
            skLineSegment(sketch, "E160.33.15.0", {"start": v(152.3, -30) * mm, "end": v(151.15, -32) * mm});
            skLineSegment(sketch, "E160.36.15.0", {"start": v(151.15, -28) * mm, "end": v(152.3, -30) * mm});
            skCircle(sketch, "E160.39.15.0", {"center": v(150, -30) * mm, "radius": 2 * mm, "construction": true});
            skLineSegment(sketch, "E160.41.15.0", {"start": v(151.73, -20) * mm, "end": v(150.87, -21.5) * mm});
            skLineSegment(sketch, "E160.44.15.0", {"start": v(148.27, -20) * mm, "end": v(149.13, -18.5) * mm});
            skLineSegment(sketch, "E160.47.15.0", {"start": v(147.7, -30) * mm, "end": v(148.85, -28) * mm});
            skCircle(sketch, "E160.50.15.0", {"center": v(150, -10) * mm, "radius": 1.25 * mm, "construction": true});
            skLineSegment(sketch, "E160.52.15.0", {"start": v(149.13, -21.5) * mm, "end": v(148.27, -20) * mm});
            skLineSegment(sketch, "E160.55.15.0", {"start": v(150.87, -18.5) * mm, "end": v(151.73, -20) * mm});
            skCircle(sketch, "E160.58.15.0", {"center": v(150, -20) * mm, "radius": 1.5 * mm, "construction": true});
            skLineSegment(sketch, "E160.60.15.0", {"start": v(150.72, -8.75) * mm, "end": v(151.44, -10) * mm});
            skSolve(sketch);
        }
        {
            var Q0;
            Q0=qSketchRegion(id+"F49",true);
            extrude(context, id + "F50", {"entities" : qUnion([Q0]), "operationType" : NewBodyOperationType.REMOVE, "depth" : 10 * mm});
        }
    });
